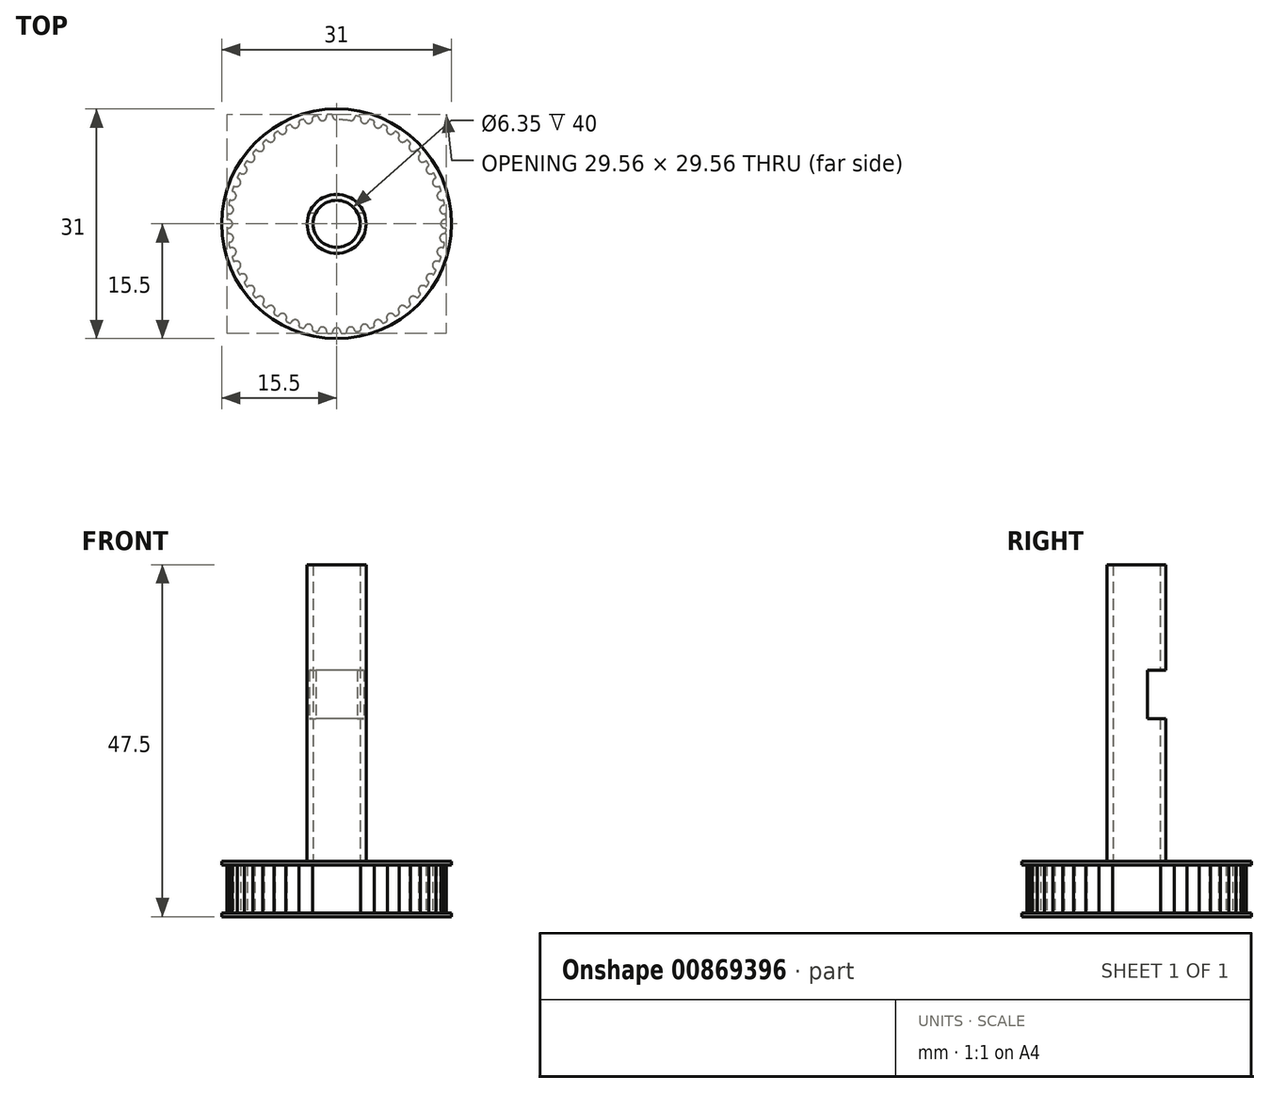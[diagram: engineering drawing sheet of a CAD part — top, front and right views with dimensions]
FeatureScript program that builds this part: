
annotation { "Feature Type Name" : "Feature", "Feature Type Description" : "" }
export const myFeature = defineFeature(function(context is Context, id is Id, definition is map)
    precondition{}
    {
        {
            var Q0;
            Q0=qCreatedBy(makeId("Top.planeOp"),FACE);
            var sketch = newSketch(context, id + "F0", { "sketchPlane" : qUnion([Q0])});
            skArc(sketch, "E0", {"start": v(-0.74, 14.78) * mm, "mid": v(-0.97, 14.77) * mm, "end": v(-1.2, 14.75) * mm});
            skCircle(sketch, "E1", {"center": v(0, 0) * mm, "radius": 14.05 * mm});
            skArc(sketch, "E2", {"start": v(-0.5, 14.37) * mm, "mid": v(-0.3, 14.14) * mm, "end": v(0, 14.05) * mm});
            skLineSegment(sketch, "E3", {"start": v(0, 0) * mm, "end": v(0.38, 14.04) * mm});
            skArc(sketch, "E4", {"start": v(-0.59, 14.65) * mm, "mid": v(-0.56, 14.5) * mm, "end": v(-0.5, 14.37) * mm});
            skArc(sketch, "E5", {"start": v(-0.59, 14.65) * mm, "mid": v(-0.64, 14.75) * mm, "end": v(-0.74, 14.78) * mm});
            skArc(sketch, "E6.MirrorCS", {"start": v(0.59, 14.65) * mm, "mid": v(0.64, 14.75) * mm, "end": v(0.74, 14.78) * mm});
            skArc(sketch, "E7.MirrorCS", {"start": v(0.59, 14.65) * mm, "mid": v(0.56, 14.5) * mm, "end": v(0.5, 14.37) * mm});
            skArc(sketch, "E8.MirrorCS", {"start": v(0.5, 14.37) * mm, "mid": v(0.3, 14.14) * mm, "end": v(0, 14.05) * mm});
            skArc(sketch, "E9.1.0", {"start": v(-2.5, 14.45) * mm, "mid": v(-2.56, 14.54) * mm, "end": v(-2.67, 14.56) * mm});
            skArc(sketch, "E9.1.1", {"start": v(-2.5, 14.45) * mm, "mid": v(-2.44, 14.31) * mm, "end": v(-2.37, 14.18) * mm});
            skArc(sketch, "E9.1.2", {"start": v(-2.37, 14.18) * mm, "mid": v(-2.14, 13.98) * mm, "end": v(-1.83, 13.93) * mm});
            skArc(sketch, "E9.1.3", {"start": v(-1.38, 14.31) * mm, "mid": v(-1.55, 14.05) * mm, "end": v(-1.83, 13.93) * mm});
            skArc(sketch, "E9.1.4", {"start": v(-1.33, 14.6) * mm, "mid": v(-1.34, 14.46) * mm, "end": v(-1.38, 14.31) * mm});
            skArc(sketch, "E9.1.5", {"start": v(-1.33, 14.6) * mm, "mid": v(-1.3, 14.7) * mm, "end": v(-1.2, 14.75) * mm});
            skArc(sketch, "E9.2.0", {"start": v(-4.36, 14) * mm, "mid": v(-4.44, 14.08) * mm, "end": v(-4.54, 14.09) * mm});
            skArc(sketch, "E9.2.1", {"start": v(-4.36, 14) * mm, "mid": v(-4.3, 13.87) * mm, "end": v(-4.2, 13.75) * mm});
            skArc(sketch, "E9.2.2", {"start": v(-4.2, 13.75) * mm, "mid": v(-3.95, 13.58) * mm, "end": v(-3.64, 13.57) * mm});
            skArc(sketch, "E9.2.3", {"start": v(-3.23, 14) * mm, "mid": v(-3.37, 13.73) * mm, "end": v(-3.64, 13.57) * mm});
            skArc(sketch, "E9.2.4", {"start": v(-3.23, 14.3) * mm, "mid": v(-3.22, 14.16) * mm, "end": v(-3.23, 14) * mm});
            skArc(sketch, "E9.2.5", {"start": v(-3.23, 14.3) * mm, "mid": v(-3.2, 14.41) * mm, "end": v(-3.1, 14.47) * mm});
            skArc(sketch, "E9.3.0", {"start": v(-6.15, 13.31) * mm, "mid": v(-6.24, 13.38) * mm, "end": v(-6.34, 13.37) * mm});
            skArc(sketch, "E9.3.1", {"start": v(-6.15, 13.31) * mm, "mid": v(-6.06, 13.2) * mm, "end": v(-5.96, 13.08) * mm});
            skArc(sketch, "E9.3.2", {"start": v(-5.96, 13.08) * mm, "mid": v(-5.68, 12.95) * mm, "end": v(-5.38, 12.98) * mm});
            skArc(sketch, "E9.3.3", {"start": v(-5.03, 13.47) * mm, "mid": v(-5.14, 13.17) * mm, "end": v(-5.38, 12.98) * mm});
            skArc(sketch, "E9.3.4", {"start": v(-5.06, 13.76) * mm, "mid": v(-5.04, 13.62) * mm, "end": v(-5.03, 13.47) * mm});
            skArc(sketch, "E9.3.5", {"start": v(-5.06, 13.76) * mm, "mid": v(-5.05, 13.87) * mm, "end": v(-4.97, 13.94) * mm});
            skArc(sketch, "E9.4.0", {"start": v(-7.83, 12.4) * mm, "mid": v(-7.93, 12.45) * mm, "end": v(-8.03, 12.43) * mm});
            skArc(sketch, "E9.4.1", {"start": v(-7.83, 12.4) * mm, "mid": v(-7.73, 12.29) * mm, "end": v(-7.62, 12.2) * mm});
            skArc(sketch, "E9.4.2", {"start": v(-7.62, 12.2) * mm, "mid": v(-7.33, 12.1) * mm, "end": v(-7.02, 12.17) * mm});
            skArc(sketch, "E9.4.3", {"start": v(-6.75, 12.7) * mm, "mid": v(-6.81, 12.4) * mm, "end": v(-7.02, 12.17) * mm});
            skArc(sketch, "E9.4.4", {"start": v(-6.82, 12.98) * mm, "mid": v(-6.77, 12.84) * mm, "end": v(-6.75, 12.7) * mm});
            skArc(sketch, "E9.4.5", {"start": v(-6.82, 12.98) * mm, "mid": v(-6.82, 13.1) * mm, "end": v(-6.75, 13.17) * mm});
            skArc(sketch, "E9.5.0", {"start": v(-9.39, 11.27) * mm, "mid": v(-9.49, 11.3) * mm, "end": v(-9.59, 11.27) * mm});
            skArc(sketch, "E9.5.1", {"start": v(-9.39, 11.27) * mm, "mid": v(-9.27, 11.17) * mm, "end": v(-9.15, 11.1) * mm});
            skArc(sketch, "E9.5.2", {"start": v(-9.15, 11.1) * mm, "mid": v(-8.84, 11.03) * mm, "end": v(-8.55, 11.15) * mm});
            skArc(sketch, "E9.5.3", {"start": v(-8.35, 11.7) * mm, "mid": v(-8.37, 11.4) * mm, "end": v(-8.55, 11.15) * mm});
            skArc(sketch, "E9.5.4", {"start": v(-8.45, 11.98) * mm, "mid": v(-8.4, 11.85) * mm, "end": v(-8.35, 11.7) * mm});
            skArc(sketch, "E9.5.5", {"start": v(-8.45, 11.98) * mm, "mid": v(-8.47, 12.09) * mm, "end": v(-8.4, 12.18) * mm});
            skArc(sketch, "E9.6.0", {"start": v(-10.78, 9.95) * mm, "mid": v(-10.88, 9.98) * mm, "end": v(-10.98, 9.93) * mm});
            skArc(sketch, "E9.6.1", {"start": v(-10.78, 9.95) * mm, "mid": v(-10.65, 9.87) * mm, "end": v(-10.52, 9.8) * mm});
            skArc(sketch, "E9.6.2", {"start": v(-10.52, 9.8) * mm, "mid": v(-10.2, 9.79) * mm, "end": v(-9.93, 9.93) * mm});
            skArc(sketch, "E9.6.3", {"start": v(-9.8, 10.52) * mm, "mid": v(-9.79, 10.2) * mm, "end": v(-9.93, 9.93) * mm});
            skArc(sketch, "E9.6.4", {"start": v(-9.95, 10.78) * mm, "mid": v(-9.87, 10.65) * mm, "end": v(-9.8, 10.52) * mm});
            skArc(sketch, "E9.6.5", {"start": v(-9.95, 10.78) * mm, "mid": v(-9.98, 10.88) * mm, "end": v(-9.93, 10.98) * mm});
            skArc(sketch, "E9.7.0", {"start": v(-11.98, 8.45) * mm, "mid": v(-12.09, 8.47) * mm, "end": v(-12.18, 8.4) * mm});
            skArc(sketch, "E9.7.1", {"start": v(-11.98, 8.45) * mm, "mid": v(-11.85, 8.4) * mm, "end": v(-11.7, 8.35) * mm});
            skArc(sketch, "E9.7.2", {"start": v(-11.7, 8.35) * mm, "mid": v(-11.4, 8.37) * mm, "end": v(-11.15, 8.55) * mm});
            skArc(sketch, "E9.7.3", {"start": v(-11.1, 9.15) * mm, "mid": v(-11.03, 8.84) * mm, "end": v(-11.15, 8.55) * mm});
            skArc(sketch, "E9.7.4", {"start": v(-11.27, 9.39) * mm, "mid": v(-11.17, 9.27) * mm, "end": v(-11.1, 9.15) * mm});
            skArc(sketch, "E9.7.5", {"start": v(-11.27, 9.39) * mm, "mid": v(-11.3, 9.49) * mm, "end": v(-11.27, 9.59) * mm});
            skArc(sketch, "E9.8.0", {"start": v(-12.98, 6.82) * mm, "mid": v(-13.1, 6.82) * mm, "end": v(-13.17, 6.75) * mm});
            skArc(sketch, "E9.8.1", {"start": v(-12.98, 6.82) * mm, "mid": v(-12.84, 6.77) * mm, "end": v(-12.7, 6.75) * mm});
            skArc(sketch, "E9.8.2", {"start": v(-12.7, 6.75) * mm, "mid": v(-12.4, 6.81) * mm, "end": v(-12.17, 7.03) * mm});
            skArc(sketch, "E9.8.3", {"start": v(-12.2, 7.62) * mm, "mid": v(-12.1, 7.33) * mm, "end": v(-12.17, 7.03) * mm});
            skArc(sketch, "E9.8.4", {"start": v(-12.4, 7.83) * mm, "mid": v(-12.29, 7.73) * mm, "end": v(-12.2, 7.62) * mm});
            skArc(sketch, "E9.8.5", {"start": v(-12.4, 7.83) * mm, "mid": v(-12.45, 7.93) * mm, "end": v(-12.43, 8.03) * mm});
            skArc(sketch, "E9.9.0", {"start": v(-13.76, 5.06) * mm, "mid": v(-13.87, 5.05) * mm, "end": v(-13.94, 4.97) * mm});
            skArc(sketch, "E9.9.1", {"start": v(-13.76, 5.06) * mm, "mid": v(-13.62, 5.04) * mm, "end": v(-13.47, 5.03) * mm});
            skArc(sketch, "E9.9.2", {"start": v(-13.47, 5.03) * mm, "mid": v(-13.17, 5.14) * mm, "end": v(-12.98, 5.38) * mm});
            skArc(sketch, "E9.9.3", {"start": v(-13.08, 5.96) * mm, "mid": v(-12.95, 5.68) * mm, "end": v(-12.98, 5.38) * mm});
            skArc(sketch, "E9.9.4", {"start": v(-13.31, 6.15) * mm, "mid": v(-13.2, 6.06) * mm, "end": v(-13.08, 5.96) * mm});
            skArc(sketch, "E9.9.5", {"start": v(-13.31, 6.15) * mm, "mid": v(-13.38, 6.24) * mm, "end": v(-13.37, 6.34) * mm});
            skArc(sketch, "E9.10.0", {"start": v(-14.3, 3.23) * mm, "mid": v(-14.41, 3.2) * mm, "end": v(-14.47, 3.1) * mm});
            skArc(sketch, "E9.10.1", {"start": v(-14.3, 3.23) * mm, "mid": v(-14.16, 3.22) * mm, "end": v(-14, 3.23) * mm});
            skArc(sketch, "E9.10.2", {"start": v(-14, 3.23) * mm, "mid": v(-13.73, 3.37) * mm, "end": v(-13.57, 3.64) * mm});
            skArc(sketch, "E9.10.3", {"start": v(-13.75, 4.2) * mm, "mid": v(-13.58, 3.95) * mm, "end": v(-13.57, 3.64) * mm});
            skArc(sketch, "E9.10.4", {"start": v(-14, 4.36) * mm, "mid": v(-13.87, 4.3) * mm, "end": v(-13.75, 4.2) * mm});
            skArc(sketch, "E9.10.5", {"start": v(-14, 4.36) * mm, "mid": v(-14.08, 4.44) * mm, "end": v(-14.09, 4.54) * mm});
            skArc(sketch, "E9.11.0", {"start": v(-14.6, 1.33) * mm, "mid": v(-14.7, 1.3) * mm, "end": v(-14.75, 1.2) * mm});
            skArc(sketch, "E9.11.1", {"start": v(-14.6, 1.33) * mm, "mid": v(-14.46, 1.34) * mm, "end": v(-14.31, 1.38) * mm});
            skArc(sketch, "E9.11.2", {"start": v(-14.31, 1.38) * mm, "mid": v(-14.05, 1.55) * mm, "end": v(-13.93, 1.83) * mm});
            skArc(sketch, "E9.11.3", {"start": v(-14.18, 2.37) * mm, "mid": v(-13.98, 2.14) * mm, "end": v(-13.93, 1.83) * mm});
            skArc(sketch, "E9.11.4", {"start": v(-14.45, 2.5) * mm, "mid": v(-14.31, 2.44) * mm, "end": v(-14.18, 2.37) * mm});
            skArc(sketch, "E9.11.5", {"start": v(-14.45, 2.5) * mm, "mid": v(-14.54, 2.56) * mm, "end": v(-14.56, 2.67) * mm});
            skArc(sketch, "E9.12.0", {"start": v(-14.65, -0.59) * mm, "mid": v(-14.75, -0.64) * mm, "end": v(-14.78, -0.74) * mm});
            skArc(sketch, "E9.12.1", {"start": v(-14.65, -0.59) * mm, "mid": v(-14.5, -0.56) * mm, "end": v(-14.37, -0.5) * mm});
            skArc(sketch, "E9.12.2", {"start": v(-14.37, -0.5) * mm, "mid": v(-14.14, -0.3) * mm, "end": v(-14.05, 0) * mm});
            skArc(sketch, "E9.12.3", {"start": v(-14.37, 0.5) * mm, "mid": v(-14.14, 0.3) * mm, "end": v(-14.05, 0) * mm});
            skArc(sketch, "E9.12.4", {"start": v(-14.65, 0.59) * mm, "mid": v(-14.5, 0.56) * mm, "end": v(-14.37, 0.5) * mm});
            skArc(sketch, "E9.12.5", {"start": v(-14.65, 0.59) * mm, "mid": v(-14.75, 0.64) * mm, "end": v(-14.78, 0.74) * mm});
            skArc(sketch, "E9.13.0", {"start": v(-14.45, -2.5) * mm, "mid": v(-14.54, -2.56) * mm, "end": v(-14.56, -2.67) * mm});
            skArc(sketch, "E9.13.1", {"start": v(-14.45, -2.5) * mm, "mid": v(-14.31, -2.44) * mm, "end": v(-14.18, -2.37) * mm});
            skArc(sketch, "E9.13.2", {"start": v(-14.18, -2.37) * mm, "mid": v(-13.98, -2.14) * mm, "end": v(-13.93, -1.83) * mm});
            skArc(sketch, "E9.13.3", {"start": v(-14.31, -1.38) * mm, "mid": v(-14.05, -1.55) * mm, "end": v(-13.93, -1.83) * mm});
            skArc(sketch, "E9.13.4", {"start": v(-14.6, -1.33) * mm, "mid": v(-14.46, -1.34) * mm, "end": v(-14.31, -1.38) * mm});
            skArc(sketch, "E9.13.5", {"start": v(-14.6, -1.33) * mm, "mid": v(-14.7, -1.3) * mm, "end": v(-14.75, -1.2) * mm});
            skArc(sketch, "E9.14.0", {"start": v(-14, -4.36) * mm, "mid": v(-14.08, -4.44) * mm, "end": v(-14.09, -4.54) * mm});
            skArc(sketch, "E9.14.1", {"start": v(-14, -4.36) * mm, "mid": v(-13.87, -4.3) * mm, "end": v(-13.75, -4.2) * mm});
            skArc(sketch, "E9.14.2", {"start": v(-13.75, -4.2) * mm, "mid": v(-13.58, -3.95) * mm, "end": v(-13.57, -3.64) * mm});
            skArc(sketch, "E9.14.3", {"start": v(-14, -3.23) * mm, "mid": v(-13.73, -3.37) * mm, "end": v(-13.57, -3.64) * mm});
            skArc(sketch, "E9.14.4", {"start": v(-14.3, -3.23) * mm, "mid": v(-14.16, -3.22) * mm, "end": v(-14, -3.23) * mm});
            skArc(sketch, "E9.14.5", {"start": v(-14.3, -3.23) * mm, "mid": v(-14.41, -3.2) * mm, "end": v(-14.47, -3.1) * mm});
            skArc(sketch, "E9.15.0", {"start": v(-13.31, -6.15) * mm, "mid": v(-13.38, -6.24) * mm, "end": v(-13.37, -6.34) * mm});
            skArc(sketch, "E9.15.1", {"start": v(-13.31, -6.15) * mm, "mid": v(-13.2, -6.06) * mm, "end": v(-13.08, -5.96) * mm});
            skArc(sketch, "E9.15.2", {"start": v(-13.08, -5.96) * mm, "mid": v(-12.95, -5.68) * mm, "end": v(-12.98, -5.38) * mm});
            skArc(sketch, "E9.15.3", {"start": v(-13.47, -5.03) * mm, "mid": v(-13.17, -5.14) * mm, "end": v(-12.98, -5.38) * mm});
            skArc(sketch, "E9.15.4", {"start": v(-13.76, -5.06) * mm, "mid": v(-13.62, -5.04) * mm, "end": v(-13.47, -5.03) * mm});
            skArc(sketch, "E9.15.5", {"start": v(-13.76, -5.06) * mm, "mid": v(-13.87, -5.05) * mm, "end": v(-13.94, -4.97) * mm});
            skArc(sketch, "E9.16.0", {"start": v(-12.4, -7.83) * mm, "mid": v(-12.45, -7.93) * mm, "end": v(-12.43, -8.03) * mm});
            skArc(sketch, "E9.16.1", {"start": v(-12.4, -7.83) * mm, "mid": v(-12.29, -7.73) * mm, "end": v(-12.2, -7.62) * mm});
            skArc(sketch, "E9.16.2", {"start": v(-12.2, -7.62) * mm, "mid": v(-12.1, -7.33) * mm, "end": v(-12.17, -7.02) * mm});
            skArc(sketch, "E9.16.3", {"start": v(-12.7, -6.75) * mm, "mid": v(-12.4, -6.81) * mm, "end": v(-12.17, -7.02) * mm});
            skArc(sketch, "E9.16.4", {"start": v(-12.98, -6.82) * mm, "mid": v(-12.84, -6.77) * mm, "end": v(-12.7, -6.75) * mm});
            skArc(sketch, "E9.16.5", {"start": v(-12.98, -6.82) * mm, "mid": v(-13.1, -6.82) * mm, "end": v(-13.17, -6.75) * mm});
            skArc(sketch, "E9.17.0", {"start": v(-11.27, -9.39) * mm, "mid": v(-11.3, -9.49) * mm, "end": v(-11.27, -9.59) * mm});
            skArc(sketch, "E9.17.1", {"start": v(-11.27, -9.39) * mm, "mid": v(-11.17, -9.27) * mm, "end": v(-11.1, -9.15) * mm});
            skArc(sketch, "E9.17.2", {"start": v(-11.1, -9.15) * mm, "mid": v(-11.03, -8.84) * mm, "end": v(-11.15, -8.55) * mm});
            skArc(sketch, "E9.17.3", {"start": v(-11.7, -8.35) * mm, "mid": v(-11.4, -8.37) * mm, "end": v(-11.15, -8.55) * mm});
            skArc(sketch, "E9.17.4", {"start": v(-11.98, -8.45) * mm, "mid": v(-11.85, -8.4) * mm, "end": v(-11.7, -8.35) * mm});
            skArc(sketch, "E9.17.5", {"start": v(-11.98, -8.45) * mm, "mid": v(-12.09, -8.47) * mm, "end": v(-12.18, -8.4) * mm});
            skArc(sketch, "E9.18.0", {"start": v(-9.95, -10.78) * mm, "mid": v(-9.98, -10.88) * mm, "end": v(-9.93, -10.98) * mm});
            skArc(sketch, "E9.18.1", {"start": v(-9.95, -10.78) * mm, "mid": v(-9.87, -10.65) * mm, "end": v(-9.8, -10.52) * mm});
            skArc(sketch, "E9.18.2", {"start": v(-9.8, -10.52) * mm, "mid": v(-9.79, -10.2) * mm, "end": v(-9.93, -9.93) * mm});
            skArc(sketch, "E9.18.3", {"start": v(-10.52, -9.8) * mm, "mid": v(-10.2, -9.79) * mm, "end": v(-9.93, -9.93) * mm});
            skArc(sketch, "E9.18.4", {"start": v(-10.78, -9.95) * mm, "mid": v(-10.65, -9.87) * mm, "end": v(-10.52, -9.8) * mm});
            skArc(sketch, "E9.18.5", {"start": v(-10.78, -9.95) * mm, "mid": v(-10.88, -9.98) * mm, "end": v(-10.98, -9.93) * mm});
            skArc(sketch, "E9.19.0", {"start": v(-8.45, -11.98) * mm, "mid": v(-8.47, -12.09) * mm, "end": v(-8.4, -12.18) * mm});
            skArc(sketch, "E9.19.1", {"start": v(-8.45, -11.98) * mm, "mid": v(-8.4, -11.85) * mm, "end": v(-8.35, -11.7) * mm});
            skArc(sketch, "E9.19.2", {"start": v(-8.35, -11.7) * mm, "mid": v(-8.37, -11.4) * mm, "end": v(-8.55, -11.15) * mm});
            skArc(sketch, "E9.19.3", {"start": v(-9.15, -11.1) * mm, "mid": v(-8.84, -11.03) * mm, "end": v(-8.55, -11.15) * mm});
            skArc(sketch, "E9.19.4", {"start": v(-9.39, -11.27) * mm, "mid": v(-9.27, -11.17) * mm, "end": v(-9.15, -11.1) * mm});
            skArc(sketch, "E9.19.5", {"start": v(-9.39, -11.27) * mm, "mid": v(-9.49, -11.3) * mm, "end": v(-9.59, -11.27) * mm});
            skArc(sketch, "E9.20.0", {"start": v(-6.82, -12.98) * mm, "mid": v(-6.82, -13.1) * mm, "end": v(-6.75, -13.17) * mm});
            skArc(sketch, "E9.20.1", {"start": v(-6.82, -12.98) * mm, "mid": v(-6.77, -12.84) * mm, "end": v(-6.75, -12.7) * mm});
            skArc(sketch, "E9.20.2", {"start": v(-6.75, -12.7) * mm, "mid": v(-6.81, -12.4) * mm, "end": v(-7.02, -12.17) * mm});
            skArc(sketch, "E9.20.3", {"start": v(-7.62, -12.2) * mm, "mid": v(-7.33, -12.1) * mm, "end": v(-7.02, -12.17) * mm});
            skArc(sketch, "E9.20.4", {"start": v(-7.83, -12.4) * mm, "mid": v(-7.73, -12.29) * mm, "end": v(-7.62, -12.2) * mm});
            skArc(sketch, "E9.20.5", {"start": v(-7.83, -12.4) * mm, "mid": v(-7.93, -12.45) * mm, "end": v(-8.03, -12.43) * mm});
            skArc(sketch, "E9.21.0", {"start": v(-5.06, -13.76) * mm, "mid": v(-5.05, -13.87) * mm, "end": v(-4.97, -13.94) * mm});
            skArc(sketch, "E9.21.1", {"start": v(-5.06, -13.76) * mm, "mid": v(-5.04, -13.62) * mm, "end": v(-5.03, -13.47) * mm});
            skArc(sketch, "E9.21.2", {"start": v(-5.03, -13.47) * mm, "mid": v(-5.14, -13.17) * mm, "end": v(-5.38, -12.98) * mm});
            skArc(sketch, "E9.21.3", {"start": v(-5.96, -13.08) * mm, "mid": v(-5.68, -12.95) * mm, "end": v(-5.38, -12.98) * mm});
            skArc(sketch, "E9.21.4", {"start": v(-6.15, -13.31) * mm, "mid": v(-6.06, -13.2) * mm, "end": v(-5.96, -13.08) * mm});
            skArc(sketch, "E9.21.5", {"start": v(-6.15, -13.31) * mm, "mid": v(-6.24, -13.38) * mm, "end": v(-6.34, -13.37) * mm});
            skArc(sketch, "E9.22.0", {"start": v(-3.23, -14.3) * mm, "mid": v(-3.2, -14.41) * mm, "end": v(-3.1, -14.47) * mm});
            skArc(sketch, "E9.22.1", {"start": v(-3.23, -14.3) * mm, "mid": v(-3.22, -14.16) * mm, "end": v(-3.23, -14) * mm});
            skArc(sketch, "E9.22.2", {"start": v(-3.23, -14) * mm, "mid": v(-3.37, -13.73) * mm, "end": v(-3.64, -13.57) * mm});
            skArc(sketch, "E9.22.3", {"start": v(-4.2, -13.75) * mm, "mid": v(-3.95, -13.58) * mm, "end": v(-3.64, -13.57) * mm});
            skArc(sketch, "E9.22.4", {"start": v(-4.36, -14) * mm, "mid": v(-4.3, -13.87) * mm, "end": v(-4.2, -13.75) * mm});
            skArc(sketch, "E9.22.5", {"start": v(-4.36, -14) * mm, "mid": v(-4.44, -14.08) * mm, "end": v(-4.54, -14.09) * mm});
            skArc(sketch, "E9.23.0", {"start": v(-1.33, -14.6) * mm, "mid": v(-1.3, -14.7) * mm, "end": v(-1.2, -14.75) * mm});
            skArc(sketch, "E9.23.1", {"start": v(-1.33, -14.6) * mm, "mid": v(-1.34, -14.46) * mm, "end": v(-1.38, -14.31) * mm});
            skArc(sketch, "E9.23.2", {"start": v(-1.38, -14.31) * mm, "mid": v(-1.55, -14.05) * mm, "end": v(-1.83, -13.93) * mm});
            skArc(sketch, "E9.23.3", {"start": v(-2.37, -14.18) * mm, "mid": v(-2.14, -13.98) * mm, "end": v(-1.83, -13.93) * mm});
            skArc(sketch, "E9.23.4", {"start": v(-2.5, -14.45) * mm, "mid": v(-2.44, -14.31) * mm, "end": v(-2.37, -14.18) * mm});
            skArc(sketch, "E9.23.5", {"start": v(-2.5, -14.45) * mm, "mid": v(-2.56, -14.54) * mm, "end": v(-2.67, -14.56) * mm});
            skArc(sketch, "E9.24.0", {"start": v(0.59, -14.65) * mm, "mid": v(0.64, -14.75) * mm, "end": v(0.74, -14.78) * mm});
            skArc(sketch, "E9.24.1", {"start": v(0.59, -14.65) * mm, "mid": v(0.56, -14.5) * mm, "end": v(0.5, -14.37) * mm});
            skArc(sketch, "E9.24.2", {"start": v(0.5, -14.37) * mm, "mid": v(0.3, -14.14) * mm, "end": v(0, -14.05) * mm});
            skArc(sketch, "E9.24.3", {"start": v(-0.5, -14.37) * mm, "mid": v(-0.3, -14.14) * mm, "end": v(0, -14.05) * mm});
            skArc(sketch, "E9.24.4", {"start": v(-0.59, -14.65) * mm, "mid": v(-0.56, -14.5) * mm, "end": v(-0.5, -14.37) * mm});
            skArc(sketch, "E9.24.5", {"start": v(-0.59, -14.65) * mm, "mid": v(-0.64, -14.75) * mm, "end": v(-0.74, -14.78) * mm});
            skArc(sketch, "E9.25.0", {"start": v(2.5, -14.45) * mm, "mid": v(2.56, -14.54) * mm, "end": v(2.67, -14.56) * mm});
            skArc(sketch, "E9.25.1", {"start": v(2.5, -14.45) * mm, "mid": v(2.44, -14.31) * mm, "end": v(2.37, -14.18) * mm});
            skArc(sketch, "E9.25.2", {"start": v(2.37, -14.18) * mm, "mid": v(2.14, -13.98) * mm, "end": v(1.83, -13.93) * mm});
            skArc(sketch, "E9.25.3", {"start": v(1.38, -14.31) * mm, "mid": v(1.55, -14.05) * mm, "end": v(1.83, -13.93) * mm});
            skArc(sketch, "E9.25.4", {"start": v(1.33, -14.6) * mm, "mid": v(1.34, -14.46) * mm, "end": v(1.38, -14.31) * mm});
            skArc(sketch, "E9.25.5", {"start": v(1.33, -14.6) * mm, "mid": v(1.3, -14.7) * mm, "end": v(1.2, -14.75) * mm});
            skArc(sketch, "E9.26.0", {"start": v(4.36, -14) * mm, "mid": v(4.44, -14.08) * mm, "end": v(4.54, -14.09) * mm});
            skArc(sketch, "E9.26.1", {"start": v(4.36, -14) * mm, "mid": v(4.3, -13.87) * mm, "end": v(4.2, -13.75) * mm});
            skArc(sketch, "E9.26.2", {"start": v(4.2, -13.75) * mm, "mid": v(3.95, -13.58) * mm, "end": v(3.64, -13.57) * mm});
            skArc(sketch, "E9.26.3", {"start": v(3.23, -14) * mm, "mid": v(3.37, -13.73) * mm, "end": v(3.64, -13.57) * mm});
            skArc(sketch, "E9.26.4", {"start": v(3.23, -14.3) * mm, "mid": v(3.22, -14.16) * mm, "end": v(3.23, -14) * mm});
            skArc(sketch, "E9.26.5", {"start": v(3.23, -14.3) * mm, "mid": v(3.2, -14.41) * mm, "end": v(3.1, -14.47) * mm});
            skArc(sketch, "E9.27.0", {"start": v(6.15, -13.31) * mm, "mid": v(6.24, -13.38) * mm, "end": v(6.34, -13.37) * mm});
            skArc(sketch, "E9.27.1", {"start": v(6.15, -13.31) * mm, "mid": v(6.06, -13.2) * mm, "end": v(5.96, -13.08) * mm});
            skArc(sketch, "E9.27.2", {"start": v(5.96, -13.08) * mm, "mid": v(5.68, -12.95) * mm, "end": v(5.38, -12.98) * mm});
            skArc(sketch, "E9.27.3", {"start": v(5.03, -13.47) * mm, "mid": v(5.14, -13.17) * mm, "end": v(5.38, -12.98) * mm});
            skArc(sketch, "E9.27.4", {"start": v(5.06, -13.76) * mm, "mid": v(5.04, -13.62) * mm, "end": v(5.03, -13.47) * mm});
            skArc(sketch, "E9.27.5", {"start": v(5.06, -13.76) * mm, "mid": v(5.05, -13.87) * mm, "end": v(4.97, -13.94) * mm});
            skArc(sketch, "E9.28.0", {"start": v(7.83, -12.4) * mm, "mid": v(7.93, -12.45) * mm, "end": v(8.03, -12.43) * mm});
            skArc(sketch, "E9.28.1", {"start": v(7.83, -12.4) * mm, "mid": v(7.73, -12.29) * mm, "end": v(7.62, -12.2) * mm});
            skArc(sketch, "E9.28.2", {"start": v(7.62, -12.2) * mm, "mid": v(7.33, -12.1) * mm, "end": v(7.02, -12.17) * mm});
            skArc(sketch, "E9.28.3", {"start": v(6.75, -12.7) * mm, "mid": v(6.81, -12.4) * mm, "end": v(7.02, -12.17) * mm});
            skArc(sketch, "E9.28.4", {"start": v(6.82, -12.98) * mm, "mid": v(6.77, -12.84) * mm, "end": v(6.75, -12.7) * mm});
            skArc(sketch, "E9.28.5", {"start": v(6.82, -12.98) * mm, "mid": v(6.82, -13.1) * mm, "end": v(6.75, -13.17) * mm});
            skArc(sketch, "E9.29.0", {"start": v(9.39, -11.27) * mm, "mid": v(9.49, -11.3) * mm, "end": v(9.59, -11.27) * mm});
            skArc(sketch, "E9.29.1", {"start": v(9.39, -11.27) * mm, "mid": v(9.27, -11.17) * mm, "end": v(9.15, -11.1) * mm});
            skArc(sketch, "E9.29.2", {"start": v(9.15, -11.1) * mm, "mid": v(8.84, -11.03) * mm, "end": v(8.55, -11.15) * mm});
            skArc(sketch, "E9.29.3", {"start": v(8.35, -11.7) * mm, "mid": v(8.37, -11.4) * mm, "end": v(8.55, -11.15) * mm});
            skArc(sketch, "E9.29.4", {"start": v(8.45, -11.98) * mm, "mid": v(8.4, -11.85) * mm, "end": v(8.35, -11.7) * mm});
            skArc(sketch, "E9.29.5", {"start": v(8.45, -11.98) * mm, "mid": v(8.47, -12.09) * mm, "end": v(8.4, -12.18) * mm});
            skArc(sketch, "E9.30.0", {"start": v(10.78, -9.95) * mm, "mid": v(10.88, -9.98) * mm, "end": v(10.98, -9.93) * mm});
            skArc(sketch, "E9.30.1", {"start": v(10.78, -9.95) * mm, "mid": v(10.65, -9.87) * mm, "end": v(10.52, -9.8) * mm});
            skArc(sketch, "E9.30.2", {"start": v(10.52, -9.8) * mm, "mid": v(10.2, -9.79) * mm, "end": v(9.93, -9.93) * mm});
            skArc(sketch, "E9.30.3", {"start": v(9.8, -10.52) * mm, "mid": v(9.79, -10.2) * mm, "end": v(9.93, -9.93) * mm});
            skArc(sketch, "E9.30.4", {"start": v(9.95, -10.78) * mm, "mid": v(9.87, -10.65) * mm, "end": v(9.8, -10.52) * mm});
            skArc(sketch, "E9.30.5", {"start": v(9.95, -10.78) * mm, "mid": v(9.98, -10.88) * mm, "end": v(9.93, -10.98) * mm});
            skArc(sketch, "E9.31.0", {"start": v(11.98, -8.45) * mm, "mid": v(12.09, -8.47) * mm, "end": v(12.18, -8.4) * mm});
            skArc(sketch, "E9.31.1", {"start": v(11.98, -8.45) * mm, "mid": v(11.85, -8.4) * mm, "end": v(11.7, -8.35) * mm});
            skArc(sketch, "E9.31.2", {"start": v(11.7, -8.35) * mm, "mid": v(11.4, -8.37) * mm, "end": v(11.15, -8.55) * mm});
            skArc(sketch, "E9.31.3", {"start": v(11.1, -9.15) * mm, "mid": v(11.03, -8.84) * mm, "end": v(11.15, -8.55) * mm});
            skArc(sketch, "E9.31.4", {"start": v(11.27, -9.39) * mm, "mid": v(11.17, -9.27) * mm, "end": v(11.1, -9.15) * mm});
            skArc(sketch, "E9.31.5", {"start": v(11.27, -9.39) * mm, "mid": v(11.3, -9.49) * mm, "end": v(11.27, -9.59) * mm});
            skArc(sketch, "E9.32.0", {"start": v(12.98, -6.82) * mm, "mid": v(13.1, -6.82) * mm, "end": v(13.17, -6.75) * mm});
            skArc(sketch, "E9.32.1", {"start": v(12.98, -6.82) * mm, "mid": v(12.84, -6.77) * mm, "end": v(12.7, -6.75) * mm});
            skArc(sketch, "E9.32.2", {"start": v(12.7, -6.75) * mm, "mid": v(12.4, -6.81) * mm, "end": v(12.17, -7.03) * mm});
            skArc(sketch, "E9.32.3", {"start": v(12.2, -7.62) * mm, "mid": v(12.1, -7.33) * mm, "end": v(12.17, -7.03) * mm});
            skArc(sketch, "E9.32.4", {"start": v(12.4, -7.83) * mm, "mid": v(12.29, -7.73) * mm, "end": v(12.2, -7.62) * mm});
            skArc(sketch, "E9.32.5", {"start": v(12.4, -7.83) * mm, "mid": v(12.45, -7.93) * mm, "end": v(12.43, -8.03) * mm});
            skArc(sketch, "E9.33.0", {"start": v(13.76, -5.06) * mm, "mid": v(13.87, -5.05) * mm, "end": v(13.94, -4.97) * mm});
            skArc(sketch, "E9.33.1", {"start": v(13.76, -5.06) * mm, "mid": v(13.62, -5.04) * mm, "end": v(13.47, -5.03) * mm});
            skArc(sketch, "E9.33.2", {"start": v(13.47, -5.03) * mm, "mid": v(13.17, -5.14) * mm, "end": v(12.98, -5.38) * mm});
            skArc(sketch, "E9.33.3", {"start": v(13.08, -5.96) * mm, "mid": v(12.95, -5.68) * mm, "end": v(12.98, -5.38) * mm});
            skArc(sketch, "E9.33.4", {"start": v(13.31, -6.15) * mm, "mid": v(13.2, -6.06) * mm, "end": v(13.08, -5.96) * mm});
            skArc(sketch, "E9.33.5", {"start": v(13.31, -6.15) * mm, "mid": v(13.38, -6.24) * mm, "end": v(13.37, -6.34) * mm});
            skArc(sketch, "E9.34.0", {"start": v(14.3, -3.23) * mm, "mid": v(14.41, -3.2) * mm, "end": v(14.47, -3.1) * mm});
            skArc(sketch, "E9.34.1", {"start": v(14.3, -3.23) * mm, "mid": v(14.16, -3.22) * mm, "end": v(14, -3.23) * mm});
            skArc(sketch, "E9.34.2", {"start": v(14, -3.23) * mm, "mid": v(13.73, -3.37) * mm, "end": v(13.57, -3.64) * mm});
            skArc(sketch, "E9.34.3", {"start": v(13.75, -4.2) * mm, "mid": v(13.58, -3.95) * mm, "end": v(13.57, -3.64) * mm});
            skArc(sketch, "E9.34.4", {"start": v(14, -4.36) * mm, "mid": v(13.87, -4.3) * mm, "end": v(13.75, -4.2) * mm});
            skArc(sketch, "E9.34.5", {"start": v(14, -4.36) * mm, "mid": v(14.08, -4.44) * mm, "end": v(14.09, -4.54) * mm});
            skArc(sketch, "E9.35.0", {"start": v(14.6, -1.33) * mm, "mid": v(14.7, -1.3) * mm, "end": v(14.75, -1.2) * mm});
            skArc(sketch, "E9.35.1", {"start": v(14.6, -1.33) * mm, "mid": v(14.46, -1.34) * mm, "end": v(14.31, -1.38) * mm});
            skArc(sketch, "E9.35.2", {"start": v(14.31, -1.38) * mm, "mid": v(14.05, -1.55) * mm, "end": v(13.93, -1.83) * mm});
            skArc(sketch, "E9.35.3", {"start": v(14.18, -2.37) * mm, "mid": v(13.98, -2.14) * mm, "end": v(13.93, -1.83) * mm});
            skArc(sketch, "E9.35.4", {"start": v(14.45, -2.5) * mm, "mid": v(14.31, -2.44) * mm, "end": v(14.18, -2.37) * mm});
            skArc(sketch, "E9.35.5", {"start": v(14.45, -2.5) * mm, "mid": v(14.54, -2.56) * mm, "end": v(14.56, -2.67) * mm});
            skArc(sketch, "E9.36.0", {"start": v(14.65, 0.59) * mm, "mid": v(14.75, 0.64) * mm, "end": v(14.78, 0.74) * mm});
            skArc(sketch, "E9.36.1", {"start": v(14.65, 0.59) * mm, "mid": v(14.5, 0.56) * mm, "end": v(14.37, 0.5) * mm});
            skArc(sketch, "E9.36.2", {"start": v(14.37, 0.5) * mm, "mid": v(14.14, 0.3) * mm, "end": v(14.05, 0) * mm});
            skArc(sketch, "E9.36.3", {"start": v(14.37, -0.5) * mm, "mid": v(14.14, -0.3) * mm, "end": v(14.05, 0) * mm});
            skArc(sketch, "E9.36.4", {"start": v(14.65, -0.59) * mm, "mid": v(14.5, -0.56) * mm, "end": v(14.37, -0.5) * mm});
            skArc(sketch, "E9.36.5", {"start": v(14.65, -0.59) * mm, "mid": v(14.75, -0.64) * mm, "end": v(14.78, -0.74) * mm});
            skArc(sketch, "E9.37.0", {"start": v(14.45, 2.5) * mm, "mid": v(14.54, 2.56) * mm, "end": v(14.56, 2.67) * mm});
            skArc(sketch, "E9.37.1", {"start": v(14.45, 2.5) * mm, "mid": v(14.31, 2.44) * mm, "end": v(14.18, 2.37) * mm});
            skArc(sketch, "E9.37.2", {"start": v(14.18, 2.37) * mm, "mid": v(13.98, 2.14) * mm, "end": v(13.93, 1.83) * mm});
            skArc(sketch, "E9.37.3", {"start": v(14.31, 1.38) * mm, "mid": v(14.05, 1.55) * mm, "end": v(13.93, 1.83) * mm});
            skArc(sketch, "E9.37.4", {"start": v(14.6, 1.33) * mm, "mid": v(14.46, 1.34) * mm, "end": v(14.31, 1.38) * mm});
            skArc(sketch, "E9.37.5", {"start": v(14.6, 1.33) * mm, "mid": v(14.7, 1.3) * mm, "end": v(14.75, 1.2) * mm});
            skArc(sketch, "E9.38.0", {"start": v(14, 4.36) * mm, "mid": v(14.08, 4.44) * mm, "end": v(14.09, 4.54) * mm});
            skArc(sketch, "E9.38.1", {"start": v(14, 4.36) * mm, "mid": v(13.87, 4.3) * mm, "end": v(13.75, 4.2) * mm});
            skArc(sketch, "E9.38.2", {"start": v(13.75, 4.2) * mm, "mid": v(13.58, 3.95) * mm, "end": v(13.57, 3.64) * mm});
            skArc(sketch, "E9.38.3", {"start": v(14, 3.23) * mm, "mid": v(13.73, 3.37) * mm, "end": v(13.57, 3.64) * mm});
            skArc(sketch, "E9.38.4", {"start": v(14.3, 3.23) * mm, "mid": v(14.16, 3.22) * mm, "end": v(14, 3.23) * mm});
            skArc(sketch, "E9.38.5", {"start": v(14.3, 3.23) * mm, "mid": v(14.41, 3.2) * mm, "end": v(14.47, 3.1) * mm});
            skArc(sketch, "E9.39.0", {"start": v(13.31, 6.15) * mm, "mid": v(13.38, 6.24) * mm, "end": v(13.37, 6.34) * mm});
            skArc(sketch, "E9.39.1", {"start": v(13.31, 6.15) * mm, "mid": v(13.2, 6.06) * mm, "end": v(13.08, 5.96) * mm});
            skArc(sketch, "E9.39.2", {"start": v(13.08, 5.96) * mm, "mid": v(12.95, 5.68) * mm, "end": v(12.98, 5.38) * mm});
            skArc(sketch, "E9.39.3", {"start": v(13.47, 5.03) * mm, "mid": v(13.17, 5.14) * mm, "end": v(12.98, 5.38) * mm});
            skArc(sketch, "E9.39.4", {"start": v(13.76, 5.06) * mm, "mid": v(13.62, 5.04) * mm, "end": v(13.47, 5.03) * mm});
            skArc(sketch, "E9.39.5", {"start": v(13.76, 5.06) * mm, "mid": v(13.87, 5.05) * mm, "end": v(13.94, 4.97) * mm});
            skArc(sketch, "E9.40.0", {"start": v(12.4, 7.83) * mm, "mid": v(12.45, 7.93) * mm, "end": v(12.43, 8.03) * mm});
            skArc(sketch, "E9.40.1", {"start": v(12.4, 7.83) * mm, "mid": v(12.29, 7.73) * mm, "end": v(12.2, 7.62) * mm});
            skArc(sketch, "E9.40.2", {"start": v(12.2, 7.62) * mm, "mid": v(12.1, 7.33) * mm, "end": v(12.17, 7.03) * mm});
            skArc(sketch, "E9.40.3", {"start": v(12.7, 6.75) * mm, "mid": v(12.4, 6.81) * mm, "end": v(12.17, 7.03) * mm});
            skArc(sketch, "E9.40.4", {"start": v(12.98, 6.82) * mm, "mid": v(12.84, 6.77) * mm, "end": v(12.7, 6.75) * mm});
            skArc(sketch, "E9.40.5", {"start": v(12.98, 6.82) * mm, "mid": v(13.1, 6.82) * mm, "end": v(13.17, 6.75) * mm});
            skArc(sketch, "E9.41.0", {"start": v(11.27, 9.39) * mm, "mid": v(11.3, 9.49) * mm, "end": v(11.27, 9.59) * mm});
            skArc(sketch, "E9.41.1", {"start": v(11.27, 9.39) * mm, "mid": v(11.17, 9.27) * mm, "end": v(11.1, 9.15) * mm});
            skArc(sketch, "E9.41.2", {"start": v(11.1, 9.15) * mm, "mid": v(11.03, 8.84) * mm, "end": v(11.15, 8.55) * mm});
            skArc(sketch, "E9.41.3", {"start": v(11.7, 8.35) * mm, "mid": v(11.4, 8.37) * mm, "end": v(11.15, 8.55) * mm});
            skArc(sketch, "E9.41.4", {"start": v(11.98, 8.45) * mm, "mid": v(11.85, 8.4) * mm, "end": v(11.7, 8.35) * mm});
            skArc(sketch, "E9.41.5", {"start": v(11.98, 8.45) * mm, "mid": v(12.09, 8.47) * mm, "end": v(12.18, 8.4) * mm});
            skArc(sketch, "E9.42.0", {"start": v(9.95, 10.78) * mm, "mid": v(9.98, 10.88) * mm, "end": v(9.93, 10.98) * mm});
            skArc(sketch, "E9.42.1", {"start": v(9.95, 10.78) * mm, "mid": v(9.87, 10.65) * mm, "end": v(9.8, 10.52) * mm});
            skArc(sketch, "E9.42.2", {"start": v(9.8, 10.52) * mm, "mid": v(9.79, 10.2) * mm, "end": v(9.93, 9.93) * mm});
            skArc(sketch, "E9.42.3", {"start": v(10.52, 9.8) * mm, "mid": v(10.2, 9.79) * mm, "end": v(9.93, 9.93) * mm});
            skArc(sketch, "E9.42.4", {"start": v(10.78, 9.95) * mm, "mid": v(10.65, 9.87) * mm, "end": v(10.52, 9.8) * mm});
            skArc(sketch, "E9.42.5", {"start": v(10.78, 9.95) * mm, "mid": v(10.88, 9.98) * mm, "end": v(10.98, 9.93) * mm});
            skArc(sketch, "E9.43.0", {"start": v(8.45, 11.98) * mm, "mid": v(8.47, 12.09) * mm, "end": v(8.4, 12.18) * mm});
            skArc(sketch, "E9.43.1", {"start": v(8.45, 11.98) * mm, "mid": v(8.4, 11.85) * mm, "end": v(8.35, 11.7) * mm});
            skArc(sketch, "E9.43.2", {"start": v(8.35, 11.7) * mm, "mid": v(8.37, 11.4) * mm, "end": v(8.55, 11.15) * mm});
            skArc(sketch, "E9.43.3", {"start": v(9.15, 11.1) * mm, "mid": v(8.84, 11.03) * mm, "end": v(8.55, 11.15) * mm});
            skArc(sketch, "E9.43.4", {"start": v(9.39, 11.27) * mm, "mid": v(9.27, 11.17) * mm, "end": v(9.15, 11.1) * mm});
            skArc(sketch, "E9.43.5", {"start": v(9.39, 11.27) * mm, "mid": v(9.49, 11.3) * mm, "end": v(9.59, 11.27) * mm});
            skArc(sketch, "E9.44.0", {"start": v(6.82, 12.98) * mm, "mid": v(6.82, 13.1) * mm, "end": v(6.75, 13.17) * mm});
            skArc(sketch, "E9.44.1", {"start": v(6.82, 12.98) * mm, "mid": v(6.77, 12.84) * mm, "end": v(6.75, 12.7) * mm});
            skArc(sketch, "E9.44.2", {"start": v(6.75, 12.7) * mm, "mid": v(6.81, 12.4) * mm, "end": v(7.03, 12.17) * mm});
            skArc(sketch, "E9.44.3", {"start": v(7.62, 12.2) * mm, "mid": v(7.33, 12.1) * mm, "end": v(7.03, 12.17) * mm});
            skArc(sketch, "E9.44.4", {"start": v(7.83, 12.4) * mm, "mid": v(7.73, 12.29) * mm, "end": v(7.62, 12.2) * mm});
            skArc(sketch, "E9.44.5", {"start": v(7.83, 12.4) * mm, "mid": v(7.93, 12.45) * mm, "end": v(8.03, 12.43) * mm});
            skArc(sketch, "E9.45.0", {"start": v(5.06, 13.76) * mm, "mid": v(5.05, 13.87) * mm, "end": v(4.97, 13.94) * mm});
            skArc(sketch, "E9.45.1", {"start": v(5.06, 13.76) * mm, "mid": v(5.04, 13.62) * mm, "end": v(5.03, 13.47) * mm});
            skArc(sketch, "E9.45.2", {"start": v(5.03, 13.47) * mm, "mid": v(5.14, 13.17) * mm, "end": v(5.38, 12.98) * mm});
            skArc(sketch, "E9.45.3", {"start": v(5.96, 13.08) * mm, "mid": v(5.68, 12.95) * mm, "end": v(5.38, 12.98) * mm});
            skArc(sketch, "E9.45.4", {"start": v(6.15, 13.31) * mm, "mid": v(6.06, 13.2) * mm, "end": v(5.96, 13.08) * mm});
            skArc(sketch, "E9.45.5", {"start": v(6.15, 13.31) * mm, "mid": v(6.24, 13.38) * mm, "end": v(6.34, 13.37) * mm});
            skArc(sketch, "E9.46.0", {"start": v(3.23, 14.3) * mm, "mid": v(3.2, 14.41) * mm, "end": v(3.1, 14.47) * mm});
            skArc(sketch, "E9.46.1", {"start": v(3.23, 14.3) * mm, "mid": v(3.22, 14.16) * mm, "end": v(3.23, 14) * mm});
            skArc(sketch, "E9.46.2", {"start": v(3.23, 14) * mm, "mid": v(3.37, 13.73) * mm, "end": v(3.64, 13.57) * mm});
            skArc(sketch, "E9.46.3", {"start": v(4.2, 13.75) * mm, "mid": v(3.95, 13.58) * mm, "end": v(3.64, 13.57) * mm});
            skArc(sketch, "E9.46.4", {"start": v(4.36, 14) * mm, "mid": v(4.3, 13.87) * mm, "end": v(4.2, 13.75) * mm});
            skArc(sketch, "E9.46.5", {"start": v(4.36, 14) * mm, "mid": v(4.44, 14.08) * mm, "end": v(4.54, 14.09) * mm});
            skArc(sketch, "E9.47.0", {"start": v(1.33, 14.6) * mm, "mid": v(1.3, 14.7) * mm, "end": v(1.2, 14.75) * mm});
            skArc(sketch, "E9.47.1", {"start": v(1.33, 14.6) * mm, "mid": v(1.34, 14.46) * mm, "end": v(1.38, 14.31) * mm});
            skArc(sketch, "E9.47.2", {"start": v(1.38, 14.31) * mm, "mid": v(1.55, 14.05) * mm, "end": v(1.83, 13.93) * mm});
            skArc(sketch, "E9.47.3", {"start": v(2.37, 14.18) * mm, "mid": v(2.14, 13.98) * mm, "end": v(1.83, 13.93) * mm});
            skArc(sketch, "E9.47.4", {"start": v(2.5, 14.45) * mm, "mid": v(2.44, 14.31) * mm, "end": v(2.37, 14.18) * mm});
            skArc(sketch, "E9.47.5", {"start": v(2.5, 14.45) * mm, "mid": v(2.56, 14.54) * mm, "end": v(2.67, 14.56) * mm});
            skArc(sketch, "E10.trimOffspring", {"start": v(1.2, 14.75) * mm, "mid": v(0.97, 14.77) * mm, "end": v(0.74, 14.78) * mm});
            skArc(sketch, "E11.trimOffspring", {"start": v(3.1, 14.47) * mm, "mid": v(2.89, 14.52) * mm, "end": v(2.67, 14.56) * mm});
            skArc(sketch, "E12.trimOffspring", {"start": v(4.97, 13.94) * mm, "mid": v(4.76, 14.01) * mm, "end": v(4.54, 14.09) * mm});
            skArc(sketch, "E13.trimOffspring", {"start": v(6.75, 13.17) * mm, "mid": v(6.55, 13.27) * mm, "end": v(6.34, 13.37) * mm});
            skArc(sketch, "E14.trimOffspring", {"start": v(8.4, 12.18) * mm, "mid": v(8.22, 12.3) * mm, "end": v(8.03, 12.43) * mm});
            skArc(sketch, "E15.trimOffspring", {"start": v(9.93, 10.98) * mm, "mid": v(9.76, 11.13) * mm, "end": v(9.59, 11.27) * mm});
            skArc(sketch, "E16.trimOffspring", {"start": v(11.27, 9.59) * mm, "mid": v(11.13, 9.76) * mm, "end": v(10.98, 9.93) * mm});
            skArc(sketch, "E17.trimOffspring", {"start": v(12.43, 8.03) * mm, "mid": v(12.3, 8.22) * mm, "end": v(12.18, 8.4) * mm});
            skArc(sketch, "E18.trimOffspring", {"start": v(13.37, 6.34) * mm, "mid": v(13.27, 6.55) * mm, "end": v(13.17, 6.75) * mm});
            skArc(sketch, "E19.trimOffspring", {"start": v(14.09, 4.54) * mm, "mid": v(14.01, 4.76) * mm, "end": v(13.94, 4.97) * mm});
            skArc(sketch, "E20.trimOffspring", {"start": v(14.56, 2.67) * mm, "mid": v(14.52, 2.89) * mm, "end": v(14.47, 3.1) * mm});
            skArc(sketch, "E21.trimOffspring", {"start": v(14.78, 0.74) * mm, "mid": v(14.77, 0.97) * mm, "end": v(14.75, 1.2) * mm});
            skArc(sketch, "E22.trimOffspring", {"start": v(14.75, -1.2) * mm, "mid": v(14.77, -0.97) * mm, "end": v(14.78, -0.74) * mm});
            skArc(sketch, "E23.trimOffspring", {"start": v(14.47, -3.1) * mm, "mid": v(14.52, -2.89) * mm, "end": v(14.56, -2.67) * mm});
            skArc(sketch, "E24.trimOffspring", {"start": v(13.94, -4.97) * mm, "mid": v(14.01, -4.76) * mm, "end": v(14.09, -4.54) * mm});
            skArc(sketch, "E25.trimOffspring", {"start": v(13.17, -6.75) * mm, "mid": v(13.27, -6.55) * mm, "end": v(13.37, -6.34) * mm});
            skArc(sketch, "E26.trimOffspring", {"start": v(12.18, -8.4) * mm, "mid": v(12.3, -8.22) * mm, "end": v(12.43, -8.03) * mm});
            skArc(sketch, "E27.trimOffspring", {"start": v(10.98, -9.93) * mm, "mid": v(11.13, -9.76) * mm, "end": v(11.27, -9.59) * mm});
            skArc(sketch, "E28.trimOffspring", {"start": v(9.59, -11.27) * mm, "mid": v(9.76, -11.13) * mm, "end": v(9.93, -10.98) * mm});
            skArc(sketch, "E29.trimOffspring", {"start": v(8.03, -12.43) * mm, "mid": v(8.22, -12.3) * mm, "end": v(8.4, -12.18) * mm});
            skArc(sketch, "E30.trimOffspring", {"start": v(6.34, -13.37) * mm, "mid": v(6.55, -13.27) * mm, "end": v(6.75, -13.17) * mm});
            skArc(sketch, "E31.trimOffspring", {"start": v(4.54, -14.09) * mm, "mid": v(4.76, -14.01) * mm, "end": v(4.97, -13.94) * mm});
            skArc(sketch, "E32.trimOffspring", {"start": v(2.67, -14.56) * mm, "mid": v(2.89, -14.52) * mm, "end": v(3.1, -14.47) * mm});
            skArc(sketch, "E33.trimOffspring", {"start": v(0.74, -14.78) * mm, "mid": v(0.97, -14.77) * mm, "end": v(1.2, -14.75) * mm});
            skArc(sketch, "E34.trimOffspring", {"start": v(-1.2, -14.75) * mm, "mid": v(-0.97, -14.77) * mm, "end": v(-0.74, -14.78) * mm});
            skArc(sketch, "E35.trimOffspring", {"start": v(-3.1, -14.47) * mm, "mid": v(-2.89, -14.52) * mm, "end": v(-2.67, -14.56) * mm});
            skArc(sketch, "E36.trimOffspring", {"start": v(-4.97, -13.94) * mm, "mid": v(-4.76, -14.01) * mm, "end": v(-4.54, -14.09) * mm});
            skArc(sketch, "E37.trimOffspring", {"start": v(-8.4, -12.18) * mm, "mid": v(-7.4, -12.82) * mm, "end": v(-6.34, -13.37) * mm});
            skArc(sketch, "E38.trimOffspring", {"start": v(-9.93, -10.98) * mm, "mid": v(-9.76, -11.13) * mm, "end": v(-9.59, -11.27) * mm});
            skArc(sketch, "E39.trimOffspring", {"start": v(-11.27, -9.59) * mm, "mid": v(-11.13, -9.76) * mm, "end": v(-10.98, -9.93) * mm});
            skArc(sketch, "E40.trimOffspring", {"start": v(-12.43, -8.03) * mm, "mid": v(-12.3, -8.22) * mm, "end": v(-12.18, -8.4) * mm});
            skArc(sketch, "E41.trimOffspring", {"start": v(-13.37, -6.34) * mm, "mid": v(-13.27, -6.55) * mm, "end": v(-13.17, -6.75) * mm});
            skArc(sketch, "E42.trimOffspring", {"start": v(-14.09, -4.54) * mm, "mid": v(-14.01, -4.76) * mm, "end": v(-13.94, -4.97) * mm});
            skArc(sketch, "E43.trimOffspring", {"start": v(-14.56, -2.67) * mm, "mid": v(-14.52, -2.89) * mm, "end": v(-14.47, -3.1) * mm});
            skArc(sketch, "E44.trimOffspring", {"start": v(-14.78, -0.74) * mm, "mid": v(-14.77, -0.97) * mm, "end": v(-14.75, -1.2) * mm});
            skArc(sketch, "E45.trimOffspring", {"start": v(-14.75, 1.2) * mm, "mid": v(-14.77, 0.97) * mm, "end": v(-14.78, 0.74) * mm});
            skArc(sketch, "E46.trimOffspring", {"start": v(-14.47, 3.1) * mm, "mid": v(-14.52, 2.89) * mm, "end": v(-14.56, 2.67) * mm});
            skArc(sketch, "E47.trimOffspring", {"start": v(-13.94, 4.97) * mm, "mid": v(-14.01, 4.76) * mm, "end": v(-14.09, 4.54) * mm});
            skArc(sketch, "E48.trimOffspring", {"start": v(-13.17, 6.75) * mm, "mid": v(-13.27, 6.55) * mm, "end": v(-13.37, 6.34) * mm});
            skArc(sketch, "E49.trimOffspring", {"start": v(-12.18, 8.4) * mm, "mid": v(-12.3, 8.22) * mm, "end": v(-12.43, 8.03) * mm});
            skArc(sketch, "E50.trimOffspring", {"start": v(-10.98, 9.93) * mm, "mid": v(-11.13, 9.76) * mm, "end": v(-11.27, 9.59) * mm});
            skArc(sketch, "E51.trimOffspring", {"start": v(-9.59, 11.27) * mm, "mid": v(-9.76, 11.13) * mm, "end": v(-9.93, 10.98) * mm});
            skArc(sketch, "E52.trimOffspring", {"start": v(-8.03, 12.43) * mm, "mid": v(-8.22, 12.3) * mm, "end": v(-8.4, 12.18) * mm});
            skArc(sketch, "E53.trimOffspring", {"start": v(-6.34, 13.37) * mm, "mid": v(-6.55, 13.27) * mm, "end": v(-6.75, 13.17) * mm});
            skArc(sketch, "E54.trimOffspring", {"start": v(-4.54, 14.09) * mm, "mid": v(-4.76, 14.01) * mm, "end": v(-4.97, 13.94) * mm});
            skArc(sketch, "E55.trimOffspring", {"start": v(-2.67, 14.56) * mm, "mid": v(-2.89, 14.52) * mm, "end": v(-3.1, 14.47) * mm});
            skSolve(sketch);
        }
        {
            var Q0;
            {var subQ0=sQuery(id+"F0.wireOp",EDGE,"E1");var subQ38=makeQuery(id+"F0.imprint","IMPRINT",VERTEX,{"derivedFrom":subQ0});Q0=makeQuery(id+"F0.imprint","IMPRINT",FACE,{"disambiguationData":[TD([[makeQuery(id+"F0.imprint","IMPRINT",EDGE,{"disambiguationData":[TD([[subQ38,1.0]])],"derivedFrom":subQ0}),1.0]])]});}
            var Q1;
            Q1=makeQuery(id+"F0.imprint","IMPRINT",FACE,{"disambiguationData":[TD([[makeQuery(id+"F0.imprint","IMPRINT",EDGE,{"derivedFrom":sQuery(id+"F0.wireOp",EDGE,"E9.4.0")}),1.0]])]});
            var Q2;
            Q2=makeQuery(id+"F0.imprint","IMPRINT",FACE,{"disambiguationData":[TD([[makeQuery(id+"F0.imprint","IMPRINT",EDGE,{"derivedFrom":sQuery(id+"F0.wireOp",EDGE,"E9.3.0")}),1.0]])]});
            var Q3;
            Q3=makeQuery(id+"F0.imprint","IMPRINT",FACE,{"disambiguationData":[TD([[makeQuery(id+"F0.imprint","IMPRINT",EDGE,{"derivedFrom":sQuery(id+"F0.wireOp",EDGE,"E9.2.0")}),1.0]])]});
            var Q4;
            Q4=makeQuery(id+"F0.imprint","IMPRINT",FACE,{"disambiguationData":[TD([[makeQuery(id+"F0.imprint","IMPRINT",EDGE,{"derivedFrom":sQuery(id+"F0.wireOp",EDGE,"E9.1.0")}),1.0]])]});
            var Q5;
            Q5=makeQuery(id+"F0.imprint","IMPRINT",FACE,{"disambiguationData":[TD([[makeQuery(id+"F0.imprint","IMPRINT",EDGE,{"derivedFrom":sQuery(id+"F0.wireOp",EDGE,"E0")}),1.0]])]});
            var Q6;
            Q6=makeQuery(id+"F0.imprint","IMPRINT",FACE,{"disambiguationData":[TD([[makeQuery(id+"F0.imprint","IMPRINT",EDGE,{"derivedFrom":sQuery(id+"F0.wireOp",EDGE,"E6.MirrorCS")}),-1.0]])]});
            var Q7;
            Q7=makeQuery(id+"F0.imprint","IMPRINT",FACE,{"disambiguationData":[TD([[makeQuery(id+"F0.imprint","IMPRINT",EDGE,{"derivedFrom":sQuery(id+"F0.wireOp",EDGE,"E9.46.0")}),1.0]])]});
            var Q8;
            Q8=makeQuery(id+"F0.imprint","IMPRINT",FACE,{"disambiguationData":[TD([[makeQuery(id+"F0.imprint","IMPRINT",EDGE,{"derivedFrom":sQuery(id+"F0.wireOp",EDGE,"E9.45.0")}),1.0]])]});
            var Q9;
            Q9=makeQuery(id+"F0.imprint","IMPRINT",FACE,{"disambiguationData":[TD([[makeQuery(id+"F0.imprint","IMPRINT",EDGE,{"derivedFrom":sQuery(id+"F0.wireOp",EDGE,"E9.44.0")}),1.0]])]});
            var Q10;
            Q10=makeQuery(id+"F0.imprint","IMPRINT",FACE,{"disambiguationData":[TD([[makeQuery(id+"F0.imprint","IMPRINT",EDGE,{"derivedFrom":sQuery(id+"F0.wireOp",EDGE,"E9.43.0")}),1.0]])]});
            var Q11;
            Q11=makeQuery(id+"F0.imprint","IMPRINT",FACE,{"disambiguationData":[TD([[makeQuery(id+"F0.imprint","IMPRINT",EDGE,{"derivedFrom":sQuery(id+"F0.wireOp",EDGE,"E9.42.0")}),1.0]])]});
            var Q12;
            Q12=makeQuery(id+"F0.imprint","IMPRINT",FACE,{"disambiguationData":[TD([[makeQuery(id+"F0.imprint","IMPRINT",EDGE,{"derivedFrom":sQuery(id+"F0.wireOp",EDGE,"E9.41.0")}),1.0]])]});
            var Q13;
            Q13=makeQuery(id+"F0.imprint","IMPRINT",FACE,{"disambiguationData":[TD([[makeQuery(id+"F0.imprint","IMPRINT",EDGE,{"derivedFrom":sQuery(id+"F0.wireOp",EDGE,"E9.40.0")}),1.0]])]});
            var Q14;
            Q14=makeQuery(id+"F0.imprint","IMPRINT",FACE,{"disambiguationData":[TD([[makeQuery(id+"F0.imprint","IMPRINT",EDGE,{"derivedFrom":sQuery(id+"F0.wireOp",EDGE,"E9.39.0")}),1.0]])]});
            var Q15;
            Q15=makeQuery(id+"F0.imprint","IMPRINT",FACE,{"disambiguationData":[TD([[makeQuery(id+"F0.imprint","IMPRINT",EDGE,{"derivedFrom":sQuery(id+"F0.wireOp",EDGE,"E9.38.0")}),1.0]])]});
            var Q16;
            Q16=makeQuery(id+"F0.imprint","IMPRINT",FACE,{"disambiguationData":[TD([[makeQuery(id+"F0.imprint","IMPRINT",EDGE,{"derivedFrom":sQuery(id+"F0.wireOp",EDGE,"E9.37.0")}),1.0]])]});
            var Q17;
            Q17=makeQuery(id+"F0.imprint","IMPRINT",FACE,{"disambiguationData":[TD([[makeQuery(id+"F0.imprint","IMPRINT",EDGE,{"derivedFrom":sQuery(id+"F0.wireOp",EDGE,"E9.36.0")}),1.0]])]});
            var Q18;
            Q18=makeQuery(id+"F0.imprint","IMPRINT",FACE,{"disambiguationData":[TD([[makeQuery(id+"F0.imprint","IMPRINT",EDGE,{"derivedFrom":sQuery(id+"F0.wireOp",EDGE,"E9.35.0")}),1.0]])]});
            var Q19;
            Q19=makeQuery(id+"F0.imprint","IMPRINT",FACE,{"disambiguationData":[TD([[makeQuery(id+"F0.imprint","IMPRINT",EDGE,{"derivedFrom":sQuery(id+"F0.wireOp",EDGE,"E9.34.0")}),1.0]])]});
            var Q20;
            Q20=makeQuery(id+"F0.imprint","IMPRINT",FACE,{"disambiguationData":[TD([[makeQuery(id+"F0.imprint","IMPRINT",EDGE,{"derivedFrom":sQuery(id+"F0.wireOp",EDGE,"E9.33.0")}),1.0]])]});
            var Q21;
            Q21=makeQuery(id+"F0.imprint","IMPRINT",FACE,{"disambiguationData":[TD([[makeQuery(id+"F0.imprint","IMPRINT",EDGE,{"derivedFrom":sQuery(id+"F0.wireOp",EDGE,"E9.32.0")}),1.0]])]});
            var Q22;
            Q22=makeQuery(id+"F0.imprint","IMPRINT",FACE,{"disambiguationData":[TD([[makeQuery(id+"F0.imprint","IMPRINT",EDGE,{"derivedFrom":sQuery(id+"F0.wireOp",EDGE,"E9.31.0")}),1.0]])]});
            var Q23;
            Q23=makeQuery(id+"F0.imprint","IMPRINT",FACE,{"disambiguationData":[TD([[makeQuery(id+"F0.imprint","IMPRINT",EDGE,{"derivedFrom":sQuery(id+"F0.wireOp",EDGE,"E9.30.0")}),1.0]])]});
            var Q24;
            Q24=makeQuery(id+"F0.imprint","IMPRINT",FACE,{"disambiguationData":[TD([[makeQuery(id+"F0.imprint","IMPRINT",EDGE,{"derivedFrom":sQuery(id+"F0.wireOp",EDGE,"E9.29.0")}),1.0]])]});
            var Q25;
            Q25=makeQuery(id+"F0.imprint","IMPRINT",FACE,{"disambiguationData":[TD([[makeQuery(id+"F0.imprint","IMPRINT",EDGE,{"derivedFrom":sQuery(id+"F0.wireOp",EDGE,"E9.28.0")}),1.0]])]});
            var Q26;
            Q26=makeQuery(id+"F0.imprint","IMPRINT",FACE,{"disambiguationData":[TD([[makeQuery(id+"F0.imprint","IMPRINT",EDGE,{"derivedFrom":sQuery(id+"F0.wireOp",EDGE,"E9.27.0")}),1.0]])]});
            var Q27;
            Q27=makeQuery(id+"F0.imprint","IMPRINT",FACE,{"disambiguationData":[TD([[makeQuery(id+"F0.imprint","IMPRINT",EDGE,{"derivedFrom":sQuery(id+"F0.wireOp",EDGE,"E9.26.0")}),1.0]])]});
            var Q28;
            Q28=makeQuery(id+"F0.imprint","IMPRINT",FACE,{"disambiguationData":[TD([[makeQuery(id+"F0.imprint","IMPRINT",EDGE,{"derivedFrom":sQuery(id+"F0.wireOp",EDGE,"E9.25.0")}),1.0]])]});
            var Q29;
            Q29=makeQuery(id+"F0.imprint","IMPRINT",FACE,{"disambiguationData":[TD([[makeQuery(id+"F0.imprint","IMPRINT",EDGE,{"derivedFrom":sQuery(id+"F0.wireOp",EDGE,"E9.24.0")}),1.0]])]});
            var Q30;
            Q30=makeQuery(id+"F0.imprint","IMPRINT",FACE,{"disambiguationData":[TD([[makeQuery(id+"F0.imprint","IMPRINT",EDGE,{"derivedFrom":sQuery(id+"F0.wireOp",EDGE,"E9.23.0")}),1.0]])]});
            var Q31;
            Q31=makeQuery(id+"F0.imprint","IMPRINT",FACE,{"disambiguationData":[TD([[makeQuery(id+"F0.imprint","IMPRINT",EDGE,{"derivedFrom":sQuery(id+"F0.wireOp",EDGE,"E9.22.0")}),1.0]])]});
            var Q32;
            Q32=makeQuery(id+"F0.imprint","IMPRINT",FACE,{"disambiguationData":[TD([[makeQuery(id+"F0.imprint","IMPRINT",EDGE,{"derivedFrom":sQuery(id+"F0.wireOp",EDGE,"E9.21.0")}),1.0]])]});
            var Q33;
            {var subQ1=sQuery(id+"F0.wireOp",EDGE,"E9.20.0");Q33=makeQuery(id+"F0.imprint","IMPRINT",FACE,{"disambiguationData":[TD([[makeQuery(id+"F0.imprint","IMPRINT",EDGE,{"derivedFrom":subQ1}),1.0]])]});}
            var Q34;
            {var subQ3=sQuery(id+"F0.wireOp",EDGE,"E9.19.0");Q34=makeQuery(id+"F0.imprint","IMPRINT",FACE,{"disambiguationData":[TD([[makeQuery(id+"F0.imprint","IMPRINT",EDGE,{"derivedFrom":subQ3}),1.0]])]});}
            var Q35;
            Q35=makeQuery(id+"F0.imprint","IMPRINT",FACE,{"disambiguationData":[TD([[makeQuery(id+"F0.imprint","IMPRINT",EDGE,{"derivedFrom":sQuery(id+"F0.wireOp",EDGE,"E9.18.0")}),1.0]])]});
            var Q36;
            Q36=makeQuery(id+"F0.imprint","IMPRINT",FACE,{"disambiguationData":[TD([[makeQuery(id+"F0.imprint","IMPRINT",EDGE,{"derivedFrom":sQuery(id+"F0.wireOp",EDGE,"E9.17.0")}),1.0]])]});
            var Q37;
            Q37=makeQuery(id+"F0.imprint","IMPRINT",FACE,{"disambiguationData":[TD([[makeQuery(id+"F0.imprint","IMPRINT",EDGE,{"derivedFrom":sQuery(id+"F0.wireOp",EDGE,"E9.16.0")}),1.0]])]});
            var Q38;
            Q38=makeQuery(id+"F0.imprint","IMPRINT",FACE,{"disambiguationData":[TD([[makeQuery(id+"F0.imprint","IMPRINT",EDGE,{"derivedFrom":sQuery(id+"F0.wireOp",EDGE,"E9.15.0")}),1.0]])]});
            var Q39;
            Q39=makeQuery(id+"F0.imprint","IMPRINT",FACE,{"disambiguationData":[TD([[makeQuery(id+"F0.imprint","IMPRINT",EDGE,{"derivedFrom":sQuery(id+"F0.wireOp",EDGE,"E9.14.0")}),1.0]])]});
            var Q40;
            Q40=makeQuery(id+"F0.imprint","IMPRINT",FACE,{"disambiguationData":[TD([[makeQuery(id+"F0.imprint","IMPRINT",EDGE,{"derivedFrom":sQuery(id+"F0.wireOp",EDGE,"E9.13.0")}),1.0]])]});
            var Q41;
            Q41=makeQuery(id+"F0.imprint","IMPRINT",FACE,{"disambiguationData":[TD([[makeQuery(id+"F0.imprint","IMPRINT",EDGE,{"derivedFrom":sQuery(id+"F0.wireOp",EDGE,"E9.12.0")}),1.0]])]});
            var Q42;
            Q42=makeQuery(id+"F0.imprint","IMPRINT",FACE,{"disambiguationData":[TD([[makeQuery(id+"F0.imprint","IMPRINT",EDGE,{"derivedFrom":sQuery(id+"F0.wireOp",EDGE,"E9.11.0")}),1.0]])]});
            var Q43;
            Q43=makeQuery(id+"F0.imprint","IMPRINT",FACE,{"disambiguationData":[TD([[makeQuery(id+"F0.imprint","IMPRINT",EDGE,{"derivedFrom":sQuery(id+"F0.wireOp",EDGE,"E9.10.0")}),1.0]])]});
            var Q44;
            Q44=makeQuery(id+"F0.imprint","IMPRINT",FACE,{"disambiguationData":[TD([[makeQuery(id+"F0.imprint","IMPRINT",EDGE,{"derivedFrom":sQuery(id+"F0.wireOp",EDGE,"E9.7.0")}),1.0]])]});
            var Q45;
            Q45=makeQuery(id+"F0.imprint","IMPRINT",FACE,{"disambiguationData":[TD([[makeQuery(id+"F0.imprint","IMPRINT",EDGE,{"derivedFrom":sQuery(id+"F0.wireOp",EDGE,"E9.6.0")}),1.0]])]});
            var Q46;
            Q46=makeQuery(id+"F0.imprint","IMPRINT",FACE,{"disambiguationData":[TD([[makeQuery(id+"F0.imprint","IMPRINT",EDGE,{"derivedFrom":sQuery(id+"F0.wireOp",EDGE,"E9.5.0")}),1.0]])]});
            var Q47;
            Q47=makeQuery(id+"F0.imprint","IMPRINT",FACE,{"disambiguationData":[TD([[makeQuery(id+"F0.imprint","IMPRINT",EDGE,{"derivedFrom":sQuery(id+"F0.wireOp",EDGE,"E9.8.0")}),1.0]])]});
            var Q48;
            Q48=makeQuery(id+"F0.imprint","IMPRINT",FACE,{"disambiguationData":[TD([[makeQuery(id+"F0.imprint","IMPRINT",EDGE,{"derivedFrom":sQuery(id+"F0.wireOp",EDGE,"E9.9.0")}),1.0]])]});
            extrude(context, id + "F1", {"entities" : qUnion([Q0, Q1, Q2, Q3, Q4, Q5, Q6, Q7, Q8, Q9, Q10, Q11, Q12, Q13, Q14, Q15, Q16, Q17, Q18, Q19, Q20, Q21, Q22, Q23, Q24, Q25, Q26, Q27, Q28, Q29, Q30, Q31, Q32, Q33, Q34, Q35, Q36, Q37, Q38, Q39, Q40, Q41, Q42, Q43, Q44, Q45, Q46, Q47, Q48]), "depth" : 6.5 * mm, "offsetDistance" : 25 * mm});
        }
        {
            var Q0;
            Q0=makeQuery(id+"F1.opExtrude","CAP_FACE",FACE,{"disambiguationData":[OSD([sQuery(id+"F0.wireOp",EDGE,"E0"),sQuery(id+"F0.wireOp",EDGE,"E2"),sQuery(id+"F0.wireOp",EDGE,"E4"),sQuery(id+"F0.wireOp",EDGE,"E5"),sQuery(id+"F0.wireOp",EDGE,"E6.MirrorCS"),sQuery(id+"F0.wireOp",EDGE,"E7.MirrorCS"),sQuery(id+"F0.wireOp",EDGE,"E8.MirrorCS"),sQuery(id+"F0.wireOp",EDGE,"E9.1.0"),sQuery(id+"F0.wireOp",EDGE,"E9.1.1"),sQuery(id+"F0.wireOp",EDGE,"E9.1.2"),sQuery(id+"F0.wireOp",EDGE,"E9.1.3"),sQuery(id+"F0.wireOp",EDGE,"E9.1.4"),sQuery(id+"F0.wireOp",EDGE,"E9.1.5"),sQuery(id+"F0.wireOp",EDGE,"E9.2.0"),sQuery(id+"F0.wireOp",EDGE,"E9.2.1"),sQuery(id+"F0.wireOp",EDGE,"E9.2.2"),sQuery(id+"F0.wireOp",EDGE,"E9.2.3"),sQuery(id+"F0.wireOp",EDGE,"E9.2.4"),sQuery(id+"F0.wireOp",EDGE,"E9.2.5"),sQuery(id+"F0.wireOp",EDGE,"E9.3.0"),sQuery(id+"F0.wireOp",EDGE,"E9.3.1"),sQuery(id+"F0.wireOp",EDGE,"E9.3.2"),sQuery(id+"F0.wireOp",EDGE,"E9.3.3"),sQuery(id+"F0.wireOp",EDGE,"E9.3.4"),sQuery(id+"F0.wireOp",EDGE,"E9.3.5"),sQuery(id+"F0.wireOp",EDGE,"E9.4.0"),sQuery(id+"F0.wireOp",EDGE,"E9.4.1"),sQuery(id+"F0.wireOp",EDGE,"E9.4.2"),sQuery(id+"F0.wireOp",EDGE,"E9.4.3"),sQuery(id+"F0.wireOp",EDGE,"E9.4.4"),sQuery(id+"F0.wireOp",EDGE,"E9.4.5"),sQuery(id+"F0.wireOp",EDGE,"E9.5.0"),sQuery(id+"F0.wireOp",EDGE,"E9.5.1"),sQuery(id+"F0.wireOp",EDGE,"E9.5.2"),sQuery(id+"F0.wireOp",EDGE,"E9.5.3"),sQuery(id+"F0.wireOp",EDGE,"E9.5.4"),sQuery(id+"F0.wireOp",EDGE,"E9.5.5"),sQuery(id+"F0.wireOp",EDGE,"E9.6.0"),sQuery(id+"F0.wireOp",EDGE,"E9.6.1"),sQuery(id+"F0.wireOp",EDGE,"E9.6.2"),sQuery(id+"F0.wireOp",EDGE,"E9.6.3"),sQuery(id+"F0.wireOp",EDGE,"E9.6.4"),sQuery(id+"F0.wireOp",EDGE,"E9.6.5"),sQuery(id+"F0.wireOp",EDGE,"E9.7.0"),sQuery(id+"F0.wireOp",EDGE,"E9.7.1"),sQuery(id+"F0.wireOp",EDGE,"E9.7.2"),sQuery(id+"F0.wireOp",EDGE,"E9.7.3"),sQuery(id+"F0.wireOp",EDGE,"E9.7.4"),sQuery(id+"F0.wireOp",EDGE,"E9.7.5"),sQuery(id+"F0.wireOp",EDGE,"E9.8.0"),sQuery(id+"F0.wireOp",EDGE,"E9.8.1"),sQuery(id+"F0.wireOp",EDGE,"E9.8.2"),sQuery(id+"F0.wireOp",EDGE,"E9.8.3"),sQuery(id+"F0.wireOp",EDGE,"E9.8.4"),sQuery(id+"F0.wireOp",EDGE,"E9.8.5"),sQuery(id+"F0.wireOp",EDGE,"E9.9.0"),sQuery(id+"F0.wireOp",EDGE,"E9.9.1"),sQuery(id+"F0.wireOp",EDGE,"E9.9.2"),sQuery(id+"F0.wireOp",EDGE,"E9.9.3"),sQuery(id+"F0.wireOp",EDGE,"E9.9.4"),sQuery(id+"F0.wireOp",EDGE,"E9.9.5"),sQuery(id+"F0.wireOp",EDGE,"E9.10.0"),sQuery(id+"F0.wireOp",EDGE,"E9.10.1"),sQuery(id+"F0.wireOp",EDGE,"E9.10.2"),sQuery(id+"F0.wireOp",EDGE,"E9.10.3"),sQuery(id+"F0.wireOp",EDGE,"E9.10.4"),sQuery(id+"F0.wireOp",EDGE,"E9.10.5"),sQuery(id+"F0.wireOp",EDGE,"E9.11.0"),sQuery(id+"F0.wireOp",EDGE,"E9.11.1"),sQuery(id+"F0.wireOp",EDGE,"E9.11.2"),sQuery(id+"F0.wireOp",EDGE,"E9.11.3"),sQuery(id+"F0.wireOp",EDGE,"E9.11.4"),sQuery(id+"F0.wireOp",EDGE,"E9.11.5"),sQuery(id+"F0.wireOp",EDGE,"E9.12.0"),sQuery(id+"F0.wireOp",EDGE,"E9.12.1"),sQuery(id+"F0.wireOp",EDGE,"E9.12.2"),sQuery(id+"F0.wireOp",EDGE,"E9.12.3"),sQuery(id+"F0.wireOp",EDGE,"E9.12.4"),sQuery(id+"F0.wireOp",EDGE,"E9.12.5"),sQuery(id+"F0.wireOp",EDGE,"E9.13.0"),sQuery(id+"F0.wireOp",EDGE,"E9.13.1"),sQuery(id+"F0.wireOp",EDGE,"E9.13.2"),sQuery(id+"F0.wireOp",EDGE,"E9.13.3"),sQuery(id+"F0.wireOp",EDGE,"E9.13.4"),sQuery(id+"F0.wireOp",EDGE,"E9.13.5"),sQuery(id+"F0.wireOp",EDGE,"E9.14.0"),sQuery(id+"F0.wireOp",EDGE,"E9.14.1"),sQuery(id+"F0.wireOp",EDGE,"E9.14.2"),sQuery(id+"F0.wireOp",EDGE,"E9.14.3"),sQuery(id+"F0.wireOp",EDGE,"E9.14.4"),sQuery(id+"F0.wireOp",EDGE,"E9.14.5"),sQuery(id+"F0.wireOp",EDGE,"E9.15.0"),sQuery(id+"F0.wireOp",EDGE,"E9.15.1"),sQuery(id+"F0.wireOp",EDGE,"E9.15.2"),sQuery(id+"F0.wireOp",EDGE,"E9.15.3"),sQuery(id+"F0.wireOp",EDGE,"E9.15.4"),sQuery(id+"F0.wireOp",EDGE,"E9.15.5"),sQuery(id+"F0.wireOp",EDGE,"E9.16.0"),sQuery(id+"F0.wireOp",EDGE,"E9.16.1"),sQuery(id+"F0.wireOp",EDGE,"E9.16.2"),sQuery(id+"F0.wireOp",EDGE,"E9.16.3"),sQuery(id+"F0.wireOp",EDGE,"E9.16.4"),sQuery(id+"F0.wireOp",EDGE,"E9.16.5"),sQuery(id+"F0.wireOp",EDGE,"E9.17.0"),sQuery(id+"F0.wireOp",EDGE,"E9.17.1"),sQuery(id+"F0.wireOp",EDGE,"E9.17.2"),sQuery(id+"F0.wireOp",EDGE,"E9.17.3"),sQuery(id+"F0.wireOp",EDGE,"E9.17.4"),sQuery(id+"F0.wireOp",EDGE,"E9.17.5"),sQuery(id+"F0.wireOp",EDGE,"E9.18.0"),sQuery(id+"F0.wireOp",EDGE,"E9.18.1"),sQuery(id+"F0.wireOp",EDGE,"E9.18.2"),sQuery(id+"F0.wireOp",EDGE,"E9.18.3"),sQuery(id+"F0.wireOp",EDGE,"E9.18.4"),sQuery(id+"F0.wireOp",EDGE,"E9.18.5"),sQuery(id+"F0.wireOp",EDGE,"E9.19.0"),sQuery(id+"F0.wireOp",EDGE,"E9.19.1"),sQuery(id+"F0.wireOp",EDGE,"E9.19.2"),sQuery(id+"F0.wireOp",EDGE,"E9.19.3"),sQuery(id+"F0.wireOp",EDGE,"E9.19.4"),sQuery(id+"F0.wireOp",EDGE,"E9.19.5"),sQuery(id+"F0.wireOp",EDGE,"E9.20.0"),sQuery(id+"F0.wireOp",EDGE,"E9.20.1"),sQuery(id+"F0.wireOp",EDGE,"E9.20.2"),sQuery(id+"F0.wireOp",EDGE,"E9.20.3"),sQuery(id+"F0.wireOp",EDGE,"E9.20.4"),sQuery(id+"F0.wireOp",EDGE,"E9.20.5"),sQuery(id+"F0.wireOp",EDGE,"E9.21.0"),sQuery(id+"F0.wireOp",EDGE,"E9.21.1"),sQuery(id+"F0.wireOp",EDGE,"E9.21.2"),sQuery(id+"F0.wireOp",EDGE,"E9.21.3"),sQuery(id+"F0.wireOp",EDGE,"E9.21.4"),sQuery(id+"F0.wireOp",EDGE,"E9.21.5"),sQuery(id+"F0.wireOp",EDGE,"E9.22.0"),sQuery(id+"F0.wireOp",EDGE,"E9.22.1"),sQuery(id+"F0.wireOp",EDGE,"E9.22.2"),sQuery(id+"F0.wireOp",EDGE,"E9.22.3"),sQuery(id+"F0.wireOp",EDGE,"E9.22.4"),sQuery(id+"F0.wireOp",EDGE,"E9.22.5"),sQuery(id+"F0.wireOp",EDGE,"E9.23.0"),sQuery(id+"F0.wireOp",EDGE,"E9.23.1"),sQuery(id+"F0.wireOp",EDGE,"E9.23.2"),sQuery(id+"F0.wireOp",EDGE,"E9.23.3"),sQuery(id+"F0.wireOp",EDGE,"E9.23.4"),sQuery(id+"F0.wireOp",EDGE,"E9.23.5"),sQuery(id+"F0.wireOp",EDGE,"E9.24.0"),sQuery(id+"F0.wireOp",EDGE,"E9.24.1"),sQuery(id+"F0.wireOp",EDGE,"E9.24.2"),sQuery(id+"F0.wireOp",EDGE,"E9.24.3"),sQuery(id+"F0.wireOp",EDGE,"E9.24.4"),sQuery(id+"F0.wireOp",EDGE,"E9.24.5"),sQuery(id+"F0.wireOp",EDGE,"E9.25.0"),sQuery(id+"F0.wireOp",EDGE,"E9.25.1"),sQuery(id+"F0.wireOp",EDGE,"E9.25.2"),sQuery(id+"F0.wireOp",EDGE,"E9.25.3"),sQuery(id+"F0.wireOp",EDGE,"E9.25.4"),sQuery(id+"F0.wireOp",EDGE,"E9.25.5"),sQuery(id+"F0.wireOp",EDGE,"E9.26.0"),sQuery(id+"F0.wireOp",EDGE,"E9.26.1"),sQuery(id+"F0.wireOp",EDGE,"E9.26.2"),sQuery(id+"F0.wireOp",EDGE,"E9.26.3"),sQuery(id+"F0.wireOp",EDGE,"E9.26.4"),sQuery(id+"F0.wireOp",EDGE,"E9.26.5"),sQuery(id+"F0.wireOp",EDGE,"E9.27.0"),sQuery(id+"F0.wireOp",EDGE,"E9.27.1"),sQuery(id+"F0.wireOp",EDGE,"E9.27.2"),sQuery(id+"F0.wireOp",EDGE,"E9.27.3"),sQuery(id+"F0.wireOp",EDGE,"E9.27.4"),sQuery(id+"F0.wireOp",EDGE,"E9.27.5"),sQuery(id+"F0.wireOp",EDGE,"E9.28.0"),sQuery(id+"F0.wireOp",EDGE,"E9.28.1"),sQuery(id+"F0.wireOp",EDGE,"E9.28.2"),sQuery(id+"F0.wireOp",EDGE,"E9.28.3"),sQuery(id+"F0.wireOp",EDGE,"E9.28.4"),sQuery(id+"F0.wireOp",EDGE,"E9.28.5"),sQuery(id+"F0.wireOp",EDGE,"E9.29.0"),sQuery(id+"F0.wireOp",EDGE,"E9.29.1"),sQuery(id+"F0.wireOp",EDGE,"E9.29.2"),sQuery(id+"F0.wireOp",EDGE,"E9.29.3"),sQuery(id+"F0.wireOp",EDGE,"E9.29.4"),sQuery(id+"F0.wireOp",EDGE,"E9.29.5"),sQuery(id+"F0.wireOp",EDGE,"E9.30.0"),sQuery(id+"F0.wireOp",EDGE,"E9.30.1"),sQuery(id+"F0.wireOp",EDGE,"E9.30.2"),sQuery(id+"F0.wireOp",EDGE,"E9.30.3"),sQuery(id+"F0.wireOp",EDGE,"E9.30.4"),sQuery(id+"F0.wireOp",EDGE,"E9.30.5"),sQuery(id+"F0.wireOp",EDGE,"E9.31.0"),sQuery(id+"F0.wireOp",EDGE,"E9.31.1"),sQuery(id+"F0.wireOp",EDGE,"E9.31.2"),sQuery(id+"F0.wireOp",EDGE,"E9.31.3"),sQuery(id+"F0.wireOp",EDGE,"E9.31.4"),sQuery(id+"F0.wireOp",EDGE,"E9.31.5"),sQuery(id+"F0.wireOp",EDGE,"E9.32.0"),sQuery(id+"F0.wireOp",EDGE,"E9.32.1"),sQuery(id+"F0.wireOp",EDGE,"E9.32.2"),sQuery(id+"F0.wireOp",EDGE,"E9.32.3"),sQuery(id+"F0.wireOp",EDGE,"E9.32.4"),sQuery(id+"F0.wireOp",EDGE,"E9.32.5"),sQuery(id+"F0.wireOp",EDGE,"E9.33.0"),sQuery(id+"F0.wireOp",EDGE,"E9.33.1"),sQuery(id+"F0.wireOp",EDGE,"E9.33.2"),sQuery(id+"F0.wireOp",EDGE,"E9.33.3"),sQuery(id+"F0.wireOp",EDGE,"E9.33.4"),sQuery(id+"F0.wireOp",EDGE,"E9.33.5"),sQuery(id+"F0.wireOp",EDGE,"E9.34.0"),sQuery(id+"F0.wireOp",EDGE,"E9.34.1"),sQuery(id+"F0.wireOp",EDGE,"E9.34.2"),sQuery(id+"F0.wireOp",EDGE,"E9.34.3"),sQuery(id+"F0.wireOp",EDGE,"E9.34.4"),sQuery(id+"F0.wireOp",EDGE,"E9.34.5"),sQuery(id+"F0.wireOp",EDGE,"E9.35.0"),sQuery(id+"F0.wireOp",EDGE,"E9.35.1"),sQuery(id+"F0.wireOp",EDGE,"E9.35.2"),sQuery(id+"F0.wireOp",EDGE,"E9.35.3"),sQuery(id+"F0.wireOp",EDGE,"E9.35.4"),sQuery(id+"F0.wireOp",EDGE,"E9.35.5"),sQuery(id+"F0.wireOp",EDGE,"E9.36.0"),sQuery(id+"F0.wireOp",EDGE,"E9.36.1"),sQuery(id+"F0.wireOp",EDGE,"E9.36.2"),sQuery(id+"F0.wireOp",EDGE,"E9.36.3"),sQuery(id+"F0.wireOp",EDGE,"E9.36.4"),sQuery(id+"F0.wireOp",EDGE,"E9.36.5"),sQuery(id+"F0.wireOp",EDGE,"E9.37.0"),sQuery(id+"F0.wireOp",EDGE,"E9.37.1"),sQuery(id+"F0.wireOp",EDGE,"E9.37.2"),sQuery(id+"F0.wireOp",EDGE,"E9.37.3"),sQuery(id+"F0.wireOp",EDGE,"E9.37.4"),sQuery(id+"F0.wireOp",EDGE,"E9.37.5"),sQuery(id+"F0.wireOp",EDGE,"E9.38.0"),sQuery(id+"F0.wireOp",EDGE,"E9.38.1"),sQuery(id+"F0.wireOp",EDGE,"E9.38.2"),sQuery(id+"F0.wireOp",EDGE,"E9.38.3"),sQuery(id+"F0.wireOp",EDGE,"E9.38.4"),sQuery(id+"F0.wireOp",EDGE,"E9.38.5"),sQuery(id+"F0.wireOp",EDGE,"E9.39.0"),sQuery(id+"F0.wireOp",EDGE,"E9.39.1"),sQuery(id+"F0.wireOp",EDGE,"E9.39.2"),sQuery(id+"F0.wireOp",EDGE,"E9.39.3"),sQuery(id+"F0.wireOp",EDGE,"E9.39.4"),sQuery(id+"F0.wireOp",EDGE,"E9.39.5"),sQuery(id+"F0.wireOp",EDGE,"E9.40.0"),sQuery(id+"F0.wireOp",EDGE,"E9.40.1"),sQuery(id+"F0.wireOp",EDGE,"E9.40.2"),sQuery(id+"F0.wireOp",EDGE,"E9.40.3"),sQuery(id+"F0.wireOp",EDGE,"E9.40.4"),sQuery(id+"F0.wireOp",EDGE,"E9.40.5"),sQuery(id+"F0.wireOp",EDGE,"E9.41.0"),sQuery(id+"F0.wireOp",EDGE,"E9.41.1"),sQuery(id+"F0.wireOp",EDGE,"E9.41.2"),sQuery(id+"F0.wireOp",EDGE,"E9.41.3"),sQuery(id+"F0.wireOp",EDGE,"E9.41.4"),sQuery(id+"F0.wireOp",EDGE,"E9.41.5"),sQuery(id+"F0.wireOp",EDGE,"E9.42.0"),sQuery(id+"F0.wireOp",EDGE,"E9.42.1"),sQuery(id+"F0.wireOp",EDGE,"E9.42.2"),sQuery(id+"F0.wireOp",EDGE,"E9.42.3"),sQuery(id+"F0.wireOp",EDGE,"E9.42.4"),sQuery(id+"F0.wireOp",EDGE,"E9.42.5"),sQuery(id+"F0.wireOp",EDGE,"E9.43.0"),sQuery(id+"F0.wireOp",EDGE,"E9.43.1"),sQuery(id+"F0.wireOp",EDGE,"E9.43.2"),sQuery(id+"F0.wireOp",EDGE,"E9.43.3"),sQuery(id+"F0.wireOp",EDGE,"E9.43.4"),sQuery(id+"F0.wireOp",EDGE,"E9.43.5"),sQuery(id+"F0.wireOp",EDGE,"E9.44.0"),sQuery(id+"F0.wireOp",EDGE,"E9.44.1"),sQuery(id+"F0.wireOp",EDGE,"E9.44.2"),sQuery(id+"F0.wireOp",EDGE,"E9.44.3"),sQuery(id+"F0.wireOp",EDGE,"E9.44.4"),sQuery(id+"F0.wireOp",EDGE,"E9.44.5"),sQuery(id+"F0.wireOp",EDGE,"E9.45.0"),sQuery(id+"F0.wireOp",EDGE,"E9.45.1"),sQuery(id+"F0.wireOp",EDGE,"E9.45.2"),sQuery(id+"F0.wireOp",EDGE,"E9.45.3"),sQuery(id+"F0.wireOp",EDGE,"E9.45.4"),sQuery(id+"F0.wireOp",EDGE,"E9.45.5"),sQuery(id+"F0.wireOp",EDGE,"E9.46.0"),sQuery(id+"F0.wireOp",EDGE,"E9.46.1"),sQuery(id+"F0.wireOp",EDGE,"E9.46.2"),sQuery(id+"F0.wireOp",EDGE,"E9.46.3"),sQuery(id+"F0.wireOp",EDGE,"E9.46.4"),sQuery(id+"F0.wireOp",EDGE,"E9.46.5"),sQuery(id+"F0.wireOp",EDGE,"E9.47.0"),sQuery(id+"F0.wireOp",EDGE,"E9.47.1"),sQuery(id+"F0.wireOp",EDGE,"E9.47.2"),sQuery(id+"F0.wireOp",EDGE,"E9.47.3"),sQuery(id+"F0.wireOp",EDGE,"E9.47.4"),sQuery(id+"F0.wireOp",EDGE,"E9.47.5"),sQuery(id+"F0.wireOp",EDGE,"E10.trimOffspring"),sQuery(id+"F0.wireOp",EDGE,"E11.trimOffspring"),sQuery(id+"F0.wireOp",EDGE,"E12.trimOffspring"),sQuery(id+"F0.wireOp",EDGE,"E13.trimOffspring"),sQuery(id+"F0.wireOp",EDGE,"E14.trimOffspring"),sQuery(id+"F0.wireOp",EDGE,"E15.trimOffspring"),sQuery(id+"F0.wireOp",EDGE,"E16.trimOffspring"),sQuery(id+"F0.wireOp",EDGE,"E17.trimOffspring"),sQuery(id+"F0.wireOp",EDGE,"E18.trimOffspring"),sQuery(id+"F0.wireOp",EDGE,"E19.trimOffspring"),sQuery(id+"F0.wireOp",EDGE,"E20.trimOffspring"),sQuery(id+"F0.wireOp",EDGE,"E21.trimOffspring"),sQuery(id+"F0.wireOp",EDGE,"E22.trimOffspring"),sQuery(id+"F0.wireOp",EDGE,"E23.trimOffspring"),sQuery(id+"F0.wireOp",EDGE,"E24.trimOffspring"),sQuery(id+"F0.wireOp",EDGE,"E25.trimOffspring"),sQuery(id+"F0.wireOp",EDGE,"E26.trimOffspring"),sQuery(id+"F0.wireOp",EDGE,"E27.trimOffspring"),sQuery(id+"F0.wireOp",EDGE,"E28.trimOffspring"),sQuery(id+"F0.wireOp",EDGE,"E29.trimOffspring"),sQuery(id+"F0.wireOp",EDGE,"E30.trimOffspring"),sQuery(id+"F0.wireOp",EDGE,"E31.trimOffspring"),sQuery(id+"F0.wireOp",EDGE,"E32.trimOffspring"),sQuery(id+"F0.wireOp",EDGE,"E33.trimOffspring"),sQuery(id+"F0.wireOp",EDGE,"E34.trimOffspring"),sQuery(id+"F0.wireOp",EDGE,"E35.trimOffspring"),sQuery(id+"F0.wireOp",EDGE,"E36.trimOffspring"),sQuery(id+"F0.wireOp",EDGE,"E37.trimOffspring"),sQuery(id+"F0.wireOp",EDGE,"E38.trimOffspring"),sQuery(id+"F0.wireOp",EDGE,"E39.trimOffspring"),sQuery(id+"F0.wireOp",EDGE,"E40.trimOffspring"),sQuery(id+"F0.wireOp",EDGE,"E41.trimOffspring"),sQuery(id+"F0.wireOp",EDGE,"E42.trimOffspring"),sQuery(id+"F0.wireOp",EDGE,"E43.trimOffspring"),sQuery(id+"F0.wireOp",EDGE,"E44.trimOffspring"),sQuery(id+"F0.wireOp",EDGE,"E45.trimOffspring"),sQuery(id+"F0.wireOp",EDGE,"E46.trimOffspring"),sQuery(id+"F0.wireOp",EDGE,"E47.trimOffspring"),sQuery(id+"F0.wireOp",EDGE,"E48.trimOffspring"),sQuery(id+"F0.wireOp",EDGE,"E49.trimOffspring"),sQuery(id+"F0.wireOp",EDGE,"E50.trimOffspring"),sQuery(id+"F0.wireOp",EDGE,"E51.trimOffspring"),sQuery(id+"F0.wireOp",EDGE,"E52.trimOffspring"),sQuery(id+"F0.wireOp",EDGE,"E53.trimOffspring"),sQuery(id+"F0.wireOp",EDGE,"E54.trimOffspring"),sQuery(id+"F0.wireOp",EDGE,"E55.trimOffspring")])],"isStart":false});
            var sketch = newSketch(context, id + "F2", { "sketchPlane" : qUnion([Q0])});
            skCircle(sketch, "E56", {"center": v(0, 0) * mm, "radius": 15.5 * mm});
            skSolve(sketch);
        }
        {
            var Q0;
            Q0=makeQuery(id+"F2.imprint","IMPRINT",FACE,{"disambiguationData":[TD([[makeQuery(id+"F2.imprint","IMPRINT",EDGE,{"derivedFrom":sQuery(id+"F2.wireOp",EDGE,"E56")}),1.0]])]});
            var Q1;
            Q1=makeQuery(id+"F2.imprint","IMPRINT",FACE,{"disambiguationData":[TD([[makeQuery(id+"F2.imprint","IMPRINT",EDGE,{"derivedFrom":makeQuery(id+"F1.opExtrude","CAP_EDGE",EDGE,{"disambiguationData":[OSD([sQuery(id+"F0.wireOp",EDGE,"E0")])],"isStart":false})}),1.0]])]});
            extrude(context, id + "F3", {"entities" : qUnion([Q0, Q1]), "operationType" : NewBodyOperationType.ADD, "depth" : .5 * mm, "offsetDistance" : 25 * mm});
        }
        {
            var Q0;
            Q0=makeQuery(id+"F1.opExtrude","CAP_FACE",FACE,{"disambiguationData":[OSD([sQuery(id+"F0.wireOp",EDGE,"E0"),sQuery(id+"F0.wireOp",EDGE,"E2"),sQuery(id+"F0.wireOp",EDGE,"E4"),sQuery(id+"F0.wireOp",EDGE,"E5"),sQuery(id+"F0.wireOp",EDGE,"E6.MirrorCS"),sQuery(id+"F0.wireOp",EDGE,"E7.MirrorCS"),sQuery(id+"F0.wireOp",EDGE,"E8.MirrorCS"),sQuery(id+"F0.wireOp",EDGE,"E9.1.0"),sQuery(id+"F0.wireOp",EDGE,"E9.1.1"),sQuery(id+"F0.wireOp",EDGE,"E9.1.2"),sQuery(id+"F0.wireOp",EDGE,"E9.1.3"),sQuery(id+"F0.wireOp",EDGE,"E9.1.4"),sQuery(id+"F0.wireOp",EDGE,"E9.1.5"),sQuery(id+"F0.wireOp",EDGE,"E9.2.0"),sQuery(id+"F0.wireOp",EDGE,"E9.2.1"),sQuery(id+"F0.wireOp",EDGE,"E9.2.2"),sQuery(id+"F0.wireOp",EDGE,"E9.2.3"),sQuery(id+"F0.wireOp",EDGE,"E9.2.4"),sQuery(id+"F0.wireOp",EDGE,"E9.2.5"),sQuery(id+"F0.wireOp",EDGE,"E9.3.0"),sQuery(id+"F0.wireOp",EDGE,"E9.3.1"),sQuery(id+"F0.wireOp",EDGE,"E9.3.2"),sQuery(id+"F0.wireOp",EDGE,"E9.3.3"),sQuery(id+"F0.wireOp",EDGE,"E9.3.4"),sQuery(id+"F0.wireOp",EDGE,"E9.3.5"),sQuery(id+"F0.wireOp",EDGE,"E9.4.0"),sQuery(id+"F0.wireOp",EDGE,"E9.4.1"),sQuery(id+"F0.wireOp",EDGE,"E9.4.2"),sQuery(id+"F0.wireOp",EDGE,"E9.4.3"),sQuery(id+"F0.wireOp",EDGE,"E9.4.4"),sQuery(id+"F0.wireOp",EDGE,"E9.4.5"),sQuery(id+"F0.wireOp",EDGE,"E9.5.0"),sQuery(id+"F0.wireOp",EDGE,"E9.5.1"),sQuery(id+"F0.wireOp",EDGE,"E9.5.2"),sQuery(id+"F0.wireOp",EDGE,"E9.5.3"),sQuery(id+"F0.wireOp",EDGE,"E9.5.4"),sQuery(id+"F0.wireOp",EDGE,"E9.5.5"),sQuery(id+"F0.wireOp",EDGE,"E9.6.0"),sQuery(id+"F0.wireOp",EDGE,"E9.6.1"),sQuery(id+"F0.wireOp",EDGE,"E9.6.2"),sQuery(id+"F0.wireOp",EDGE,"E9.6.3"),sQuery(id+"F0.wireOp",EDGE,"E9.6.4"),sQuery(id+"F0.wireOp",EDGE,"E9.6.5"),sQuery(id+"F0.wireOp",EDGE,"E9.7.0"),sQuery(id+"F0.wireOp",EDGE,"E9.7.1"),sQuery(id+"F0.wireOp",EDGE,"E9.7.2"),sQuery(id+"F0.wireOp",EDGE,"E9.7.3"),sQuery(id+"F0.wireOp",EDGE,"E9.7.4"),sQuery(id+"F0.wireOp",EDGE,"E9.7.5"),sQuery(id+"F0.wireOp",EDGE,"E9.8.0"),sQuery(id+"F0.wireOp",EDGE,"E9.8.1"),sQuery(id+"F0.wireOp",EDGE,"E9.8.2"),sQuery(id+"F0.wireOp",EDGE,"E9.8.3"),sQuery(id+"F0.wireOp",EDGE,"E9.8.4"),sQuery(id+"F0.wireOp",EDGE,"E9.8.5"),sQuery(id+"F0.wireOp",EDGE,"E9.9.0"),sQuery(id+"F0.wireOp",EDGE,"E9.9.1"),sQuery(id+"F0.wireOp",EDGE,"E9.9.2"),sQuery(id+"F0.wireOp",EDGE,"E9.9.3"),sQuery(id+"F0.wireOp",EDGE,"E9.9.4"),sQuery(id+"F0.wireOp",EDGE,"E9.9.5"),sQuery(id+"F0.wireOp",EDGE,"E9.10.0"),sQuery(id+"F0.wireOp",EDGE,"E9.10.1"),sQuery(id+"F0.wireOp",EDGE,"E9.10.2"),sQuery(id+"F0.wireOp",EDGE,"E9.10.3"),sQuery(id+"F0.wireOp",EDGE,"E9.10.4"),sQuery(id+"F0.wireOp",EDGE,"E9.10.5"),sQuery(id+"F0.wireOp",EDGE,"E9.11.0"),sQuery(id+"F0.wireOp",EDGE,"E9.11.1"),sQuery(id+"F0.wireOp",EDGE,"E9.11.2"),sQuery(id+"F0.wireOp",EDGE,"E9.11.3"),sQuery(id+"F0.wireOp",EDGE,"E9.11.4"),sQuery(id+"F0.wireOp",EDGE,"E9.11.5"),sQuery(id+"F0.wireOp",EDGE,"E9.12.0"),sQuery(id+"F0.wireOp",EDGE,"E9.12.1"),sQuery(id+"F0.wireOp",EDGE,"E9.12.2"),sQuery(id+"F0.wireOp",EDGE,"E9.12.3"),sQuery(id+"F0.wireOp",EDGE,"E9.12.4"),sQuery(id+"F0.wireOp",EDGE,"E9.12.5"),sQuery(id+"F0.wireOp",EDGE,"E9.13.0"),sQuery(id+"F0.wireOp",EDGE,"E9.13.1"),sQuery(id+"F0.wireOp",EDGE,"E9.13.2"),sQuery(id+"F0.wireOp",EDGE,"E9.13.3"),sQuery(id+"F0.wireOp",EDGE,"E9.13.4"),sQuery(id+"F0.wireOp",EDGE,"E9.13.5"),sQuery(id+"F0.wireOp",EDGE,"E9.14.0"),sQuery(id+"F0.wireOp",EDGE,"E9.14.1"),sQuery(id+"F0.wireOp",EDGE,"E9.14.2"),sQuery(id+"F0.wireOp",EDGE,"E9.14.3"),sQuery(id+"F0.wireOp",EDGE,"E9.14.4"),sQuery(id+"F0.wireOp",EDGE,"E9.14.5"),sQuery(id+"F0.wireOp",EDGE,"E9.15.0"),sQuery(id+"F0.wireOp",EDGE,"E9.15.1"),sQuery(id+"F0.wireOp",EDGE,"E9.15.2"),sQuery(id+"F0.wireOp",EDGE,"E9.15.3"),sQuery(id+"F0.wireOp",EDGE,"E9.15.4"),sQuery(id+"F0.wireOp",EDGE,"E9.15.5"),sQuery(id+"F0.wireOp",EDGE,"E9.16.0"),sQuery(id+"F0.wireOp",EDGE,"E9.16.1"),sQuery(id+"F0.wireOp",EDGE,"E9.16.2"),sQuery(id+"F0.wireOp",EDGE,"E9.16.3"),sQuery(id+"F0.wireOp",EDGE,"E9.16.4"),sQuery(id+"F0.wireOp",EDGE,"E9.16.5"),sQuery(id+"F0.wireOp",EDGE,"E9.17.0"),sQuery(id+"F0.wireOp",EDGE,"E9.17.1"),sQuery(id+"F0.wireOp",EDGE,"E9.17.2"),sQuery(id+"F0.wireOp",EDGE,"E9.17.3"),sQuery(id+"F0.wireOp",EDGE,"E9.17.4"),sQuery(id+"F0.wireOp",EDGE,"E9.17.5"),sQuery(id+"F0.wireOp",EDGE,"E9.18.0"),sQuery(id+"F0.wireOp",EDGE,"E9.18.1"),sQuery(id+"F0.wireOp",EDGE,"E9.18.2"),sQuery(id+"F0.wireOp",EDGE,"E9.18.3"),sQuery(id+"F0.wireOp",EDGE,"E9.18.4"),sQuery(id+"F0.wireOp",EDGE,"E9.18.5"),sQuery(id+"F0.wireOp",EDGE,"E9.19.0"),sQuery(id+"F0.wireOp",EDGE,"E9.19.1"),sQuery(id+"F0.wireOp",EDGE,"E9.19.2"),sQuery(id+"F0.wireOp",EDGE,"E9.19.3"),sQuery(id+"F0.wireOp",EDGE,"E9.19.4"),sQuery(id+"F0.wireOp",EDGE,"E9.19.5"),sQuery(id+"F0.wireOp",EDGE,"E9.20.0"),sQuery(id+"F0.wireOp",EDGE,"E9.20.1"),sQuery(id+"F0.wireOp",EDGE,"E9.20.2"),sQuery(id+"F0.wireOp",EDGE,"E9.20.3"),sQuery(id+"F0.wireOp",EDGE,"E9.20.4"),sQuery(id+"F0.wireOp",EDGE,"E9.20.5"),sQuery(id+"F0.wireOp",EDGE,"E9.21.0"),sQuery(id+"F0.wireOp",EDGE,"E9.21.1"),sQuery(id+"F0.wireOp",EDGE,"E9.21.2"),sQuery(id+"F0.wireOp",EDGE,"E9.21.3"),sQuery(id+"F0.wireOp",EDGE,"E9.21.4"),sQuery(id+"F0.wireOp",EDGE,"E9.21.5"),sQuery(id+"F0.wireOp",EDGE,"E9.22.0"),sQuery(id+"F0.wireOp",EDGE,"E9.22.1"),sQuery(id+"F0.wireOp",EDGE,"E9.22.2"),sQuery(id+"F0.wireOp",EDGE,"E9.22.3"),sQuery(id+"F0.wireOp",EDGE,"E9.22.4"),sQuery(id+"F0.wireOp",EDGE,"E9.22.5"),sQuery(id+"F0.wireOp",EDGE,"E9.23.0"),sQuery(id+"F0.wireOp",EDGE,"E9.23.1"),sQuery(id+"F0.wireOp",EDGE,"E9.23.2"),sQuery(id+"F0.wireOp",EDGE,"E9.23.3"),sQuery(id+"F0.wireOp",EDGE,"E9.23.4"),sQuery(id+"F0.wireOp",EDGE,"E9.23.5"),sQuery(id+"F0.wireOp",EDGE,"E9.24.0"),sQuery(id+"F0.wireOp",EDGE,"E9.24.1"),sQuery(id+"F0.wireOp",EDGE,"E9.24.2"),sQuery(id+"F0.wireOp",EDGE,"E9.24.3"),sQuery(id+"F0.wireOp",EDGE,"E9.24.4"),sQuery(id+"F0.wireOp",EDGE,"E9.24.5"),sQuery(id+"F0.wireOp",EDGE,"E9.25.0"),sQuery(id+"F0.wireOp",EDGE,"E9.25.1"),sQuery(id+"F0.wireOp",EDGE,"E9.25.2"),sQuery(id+"F0.wireOp",EDGE,"E9.25.3"),sQuery(id+"F0.wireOp",EDGE,"E9.25.4"),sQuery(id+"F0.wireOp",EDGE,"E9.25.5"),sQuery(id+"F0.wireOp",EDGE,"E9.26.0"),sQuery(id+"F0.wireOp",EDGE,"E9.26.1"),sQuery(id+"F0.wireOp",EDGE,"E9.26.2"),sQuery(id+"F0.wireOp",EDGE,"E9.26.3"),sQuery(id+"F0.wireOp",EDGE,"E9.26.4"),sQuery(id+"F0.wireOp",EDGE,"E9.26.5"),sQuery(id+"F0.wireOp",EDGE,"E9.27.0"),sQuery(id+"F0.wireOp",EDGE,"E9.27.1"),sQuery(id+"F0.wireOp",EDGE,"E9.27.2"),sQuery(id+"F0.wireOp",EDGE,"E9.27.3"),sQuery(id+"F0.wireOp",EDGE,"E9.27.4"),sQuery(id+"F0.wireOp",EDGE,"E9.27.5"),sQuery(id+"F0.wireOp",EDGE,"E9.28.0"),sQuery(id+"F0.wireOp",EDGE,"E9.28.1"),sQuery(id+"F0.wireOp",EDGE,"E9.28.2"),sQuery(id+"F0.wireOp",EDGE,"E9.28.3"),sQuery(id+"F0.wireOp",EDGE,"E9.28.4"),sQuery(id+"F0.wireOp",EDGE,"E9.28.5"),sQuery(id+"F0.wireOp",EDGE,"E9.29.0"),sQuery(id+"F0.wireOp",EDGE,"E9.29.1"),sQuery(id+"F0.wireOp",EDGE,"E9.29.2"),sQuery(id+"F0.wireOp",EDGE,"E9.29.3"),sQuery(id+"F0.wireOp",EDGE,"E9.29.4"),sQuery(id+"F0.wireOp",EDGE,"E9.29.5"),sQuery(id+"F0.wireOp",EDGE,"E9.30.0"),sQuery(id+"F0.wireOp",EDGE,"E9.30.1"),sQuery(id+"F0.wireOp",EDGE,"E9.30.2"),sQuery(id+"F0.wireOp",EDGE,"E9.30.3"),sQuery(id+"F0.wireOp",EDGE,"E9.30.4"),sQuery(id+"F0.wireOp",EDGE,"E9.30.5"),sQuery(id+"F0.wireOp",EDGE,"E9.31.0"),sQuery(id+"F0.wireOp",EDGE,"E9.31.1"),sQuery(id+"F0.wireOp",EDGE,"E9.31.2"),sQuery(id+"F0.wireOp",EDGE,"E9.31.3"),sQuery(id+"F0.wireOp",EDGE,"E9.31.4"),sQuery(id+"F0.wireOp",EDGE,"E9.31.5"),sQuery(id+"F0.wireOp",EDGE,"E9.32.0"),sQuery(id+"F0.wireOp",EDGE,"E9.32.1"),sQuery(id+"F0.wireOp",EDGE,"E9.32.2"),sQuery(id+"F0.wireOp",EDGE,"E9.32.3"),sQuery(id+"F0.wireOp",EDGE,"E9.32.4"),sQuery(id+"F0.wireOp",EDGE,"E9.32.5"),sQuery(id+"F0.wireOp",EDGE,"E9.33.0"),sQuery(id+"F0.wireOp",EDGE,"E9.33.1"),sQuery(id+"F0.wireOp",EDGE,"E9.33.2"),sQuery(id+"F0.wireOp",EDGE,"E9.33.3"),sQuery(id+"F0.wireOp",EDGE,"E9.33.4"),sQuery(id+"F0.wireOp",EDGE,"E9.33.5"),sQuery(id+"F0.wireOp",EDGE,"E9.34.0"),sQuery(id+"F0.wireOp",EDGE,"E9.34.1"),sQuery(id+"F0.wireOp",EDGE,"E9.34.2"),sQuery(id+"F0.wireOp",EDGE,"E9.34.3"),sQuery(id+"F0.wireOp",EDGE,"E9.34.4"),sQuery(id+"F0.wireOp",EDGE,"E9.34.5"),sQuery(id+"F0.wireOp",EDGE,"E9.35.0"),sQuery(id+"F0.wireOp",EDGE,"E9.35.1"),sQuery(id+"F0.wireOp",EDGE,"E9.35.2"),sQuery(id+"F0.wireOp",EDGE,"E9.35.3"),sQuery(id+"F0.wireOp",EDGE,"E9.35.4"),sQuery(id+"F0.wireOp",EDGE,"E9.35.5"),sQuery(id+"F0.wireOp",EDGE,"E9.36.0"),sQuery(id+"F0.wireOp",EDGE,"E9.36.1"),sQuery(id+"F0.wireOp",EDGE,"E9.36.2"),sQuery(id+"F0.wireOp",EDGE,"E9.36.3"),sQuery(id+"F0.wireOp",EDGE,"E9.36.4"),sQuery(id+"F0.wireOp",EDGE,"E9.36.5"),sQuery(id+"F0.wireOp",EDGE,"E9.37.0"),sQuery(id+"F0.wireOp",EDGE,"E9.37.1"),sQuery(id+"F0.wireOp",EDGE,"E9.37.2"),sQuery(id+"F0.wireOp",EDGE,"E9.37.3"),sQuery(id+"F0.wireOp",EDGE,"E9.37.4"),sQuery(id+"F0.wireOp",EDGE,"E9.37.5"),sQuery(id+"F0.wireOp",EDGE,"E9.38.0"),sQuery(id+"F0.wireOp",EDGE,"E9.38.1"),sQuery(id+"F0.wireOp",EDGE,"E9.38.2"),sQuery(id+"F0.wireOp",EDGE,"E9.38.3"),sQuery(id+"F0.wireOp",EDGE,"E9.38.4"),sQuery(id+"F0.wireOp",EDGE,"E9.38.5"),sQuery(id+"F0.wireOp",EDGE,"E9.39.0"),sQuery(id+"F0.wireOp",EDGE,"E9.39.1"),sQuery(id+"F0.wireOp",EDGE,"E9.39.2"),sQuery(id+"F0.wireOp",EDGE,"E9.39.3"),sQuery(id+"F0.wireOp",EDGE,"E9.39.4"),sQuery(id+"F0.wireOp",EDGE,"E9.39.5"),sQuery(id+"F0.wireOp",EDGE,"E9.40.0"),sQuery(id+"F0.wireOp",EDGE,"E9.40.1"),sQuery(id+"F0.wireOp",EDGE,"E9.40.2"),sQuery(id+"F0.wireOp",EDGE,"E9.40.3"),sQuery(id+"F0.wireOp",EDGE,"E9.40.4"),sQuery(id+"F0.wireOp",EDGE,"E9.40.5"),sQuery(id+"F0.wireOp",EDGE,"E9.41.0"),sQuery(id+"F0.wireOp",EDGE,"E9.41.1"),sQuery(id+"F0.wireOp",EDGE,"E9.41.2"),sQuery(id+"F0.wireOp",EDGE,"E9.41.3"),sQuery(id+"F0.wireOp",EDGE,"E9.41.4"),sQuery(id+"F0.wireOp",EDGE,"E9.41.5"),sQuery(id+"F0.wireOp",EDGE,"E9.42.0"),sQuery(id+"F0.wireOp",EDGE,"E9.42.1"),sQuery(id+"F0.wireOp",EDGE,"E9.42.2"),sQuery(id+"F0.wireOp",EDGE,"E9.42.3"),sQuery(id+"F0.wireOp",EDGE,"E9.42.4"),sQuery(id+"F0.wireOp",EDGE,"E9.42.5"),sQuery(id+"F0.wireOp",EDGE,"E9.43.0"),sQuery(id+"F0.wireOp",EDGE,"E9.43.1"),sQuery(id+"F0.wireOp",EDGE,"E9.43.2"),sQuery(id+"F0.wireOp",EDGE,"E9.43.3"),sQuery(id+"F0.wireOp",EDGE,"E9.43.4"),sQuery(id+"F0.wireOp",EDGE,"E9.43.5"),sQuery(id+"F0.wireOp",EDGE,"E9.44.0"),sQuery(id+"F0.wireOp",EDGE,"E9.44.1"),sQuery(id+"F0.wireOp",EDGE,"E9.44.2"),sQuery(id+"F0.wireOp",EDGE,"E9.44.3"),sQuery(id+"F0.wireOp",EDGE,"E9.44.4"),sQuery(id+"F0.wireOp",EDGE,"E9.44.5"),sQuery(id+"F0.wireOp",EDGE,"E9.45.0"),sQuery(id+"F0.wireOp",EDGE,"E9.45.1"),sQuery(id+"F0.wireOp",EDGE,"E9.45.2"),sQuery(id+"F0.wireOp",EDGE,"E9.45.3"),sQuery(id+"F0.wireOp",EDGE,"E9.45.4"),sQuery(id+"F0.wireOp",EDGE,"E9.45.5"),sQuery(id+"F0.wireOp",EDGE,"E9.46.0"),sQuery(id+"F0.wireOp",EDGE,"E9.46.1"),sQuery(id+"F0.wireOp",EDGE,"E9.46.2"),sQuery(id+"F0.wireOp",EDGE,"E9.46.3"),sQuery(id+"F0.wireOp",EDGE,"E9.46.4"),sQuery(id+"F0.wireOp",EDGE,"E9.46.5"),sQuery(id+"F0.wireOp",EDGE,"E9.47.0"),sQuery(id+"F0.wireOp",EDGE,"E9.47.1"),sQuery(id+"F0.wireOp",EDGE,"E9.47.2"),sQuery(id+"F0.wireOp",EDGE,"E9.47.3"),sQuery(id+"F0.wireOp",EDGE,"E9.47.4"),sQuery(id+"F0.wireOp",EDGE,"E9.47.5"),sQuery(id+"F0.wireOp",EDGE,"E10.trimOffspring"),sQuery(id+"F0.wireOp",EDGE,"E11.trimOffspring"),sQuery(id+"F0.wireOp",EDGE,"E12.trimOffspring"),sQuery(id+"F0.wireOp",EDGE,"E13.trimOffspring"),sQuery(id+"F0.wireOp",EDGE,"E14.trimOffspring"),sQuery(id+"F0.wireOp",EDGE,"E15.trimOffspring"),sQuery(id+"F0.wireOp",EDGE,"E16.trimOffspring"),sQuery(id+"F0.wireOp",EDGE,"E17.trimOffspring"),sQuery(id+"F0.wireOp",EDGE,"E18.trimOffspring"),sQuery(id+"F0.wireOp",EDGE,"E19.trimOffspring"),sQuery(id+"F0.wireOp",EDGE,"E20.trimOffspring"),sQuery(id+"F0.wireOp",EDGE,"E21.trimOffspring"),sQuery(id+"F0.wireOp",EDGE,"E22.trimOffspring"),sQuery(id+"F0.wireOp",EDGE,"E23.trimOffspring"),sQuery(id+"F0.wireOp",EDGE,"E24.trimOffspring"),sQuery(id+"F0.wireOp",EDGE,"E25.trimOffspring"),sQuery(id+"F0.wireOp",EDGE,"E26.trimOffspring"),sQuery(id+"F0.wireOp",EDGE,"E27.trimOffspring"),sQuery(id+"F0.wireOp",EDGE,"E28.trimOffspring"),sQuery(id+"F0.wireOp",EDGE,"E29.trimOffspring"),sQuery(id+"F0.wireOp",EDGE,"E30.trimOffspring"),sQuery(id+"F0.wireOp",EDGE,"E31.trimOffspring"),sQuery(id+"F0.wireOp",EDGE,"E32.trimOffspring"),sQuery(id+"F0.wireOp",EDGE,"E33.trimOffspring"),sQuery(id+"F0.wireOp",EDGE,"E34.trimOffspring"),sQuery(id+"F0.wireOp",EDGE,"E35.trimOffspring"),sQuery(id+"F0.wireOp",EDGE,"E36.trimOffspring"),sQuery(id+"F0.wireOp",EDGE,"E37.trimOffspring"),sQuery(id+"F0.wireOp",EDGE,"E38.trimOffspring"),sQuery(id+"F0.wireOp",EDGE,"E39.trimOffspring"),sQuery(id+"F0.wireOp",EDGE,"E40.trimOffspring"),sQuery(id+"F0.wireOp",EDGE,"E41.trimOffspring"),sQuery(id+"F0.wireOp",EDGE,"E42.trimOffspring"),sQuery(id+"F0.wireOp",EDGE,"E43.trimOffspring"),sQuery(id+"F0.wireOp",EDGE,"E44.trimOffspring"),sQuery(id+"F0.wireOp",EDGE,"E45.trimOffspring"),sQuery(id+"F0.wireOp",EDGE,"E46.trimOffspring"),sQuery(id+"F0.wireOp",EDGE,"E47.trimOffspring"),sQuery(id+"F0.wireOp",EDGE,"E48.trimOffspring"),sQuery(id+"F0.wireOp",EDGE,"E49.trimOffspring"),sQuery(id+"F0.wireOp",EDGE,"E50.trimOffspring"),sQuery(id+"F0.wireOp",EDGE,"E51.trimOffspring"),sQuery(id+"F0.wireOp",EDGE,"E52.trimOffspring"),sQuery(id+"F0.wireOp",EDGE,"E53.trimOffspring"),sQuery(id+"F0.wireOp",EDGE,"E54.trimOffspring"),sQuery(id+"F0.wireOp",EDGE,"E55.trimOffspring")])],"isStart":true});
            var sketch = newSketch(context, id + "F4", { "sketchPlane" : qUnion([Q0])});
            skCircle(sketch, "E57", {"center": v(0, 0) * mm, "radius": 15.5 * mm});
            skSolve(sketch);
        }
        {
            var Q0;
            Q0=makeQuery(id+"F4.imprint","IMPRINT",FACE,{"disambiguationData":[TD([[makeQuery(id+"F4.imprint","IMPRINT",EDGE,{"derivedFrom":makeQuery(id+"F1.opExtrude","CAP_EDGE",EDGE,{"disambiguationData":[OSD([sQuery(id+"F0.wireOp",EDGE,"E0")])],"isStart":true})}),-1.0]])]});
            var Q1;
            Q1=makeQuery(id+"F4.imprint","IMPRINT",FACE,{"disambiguationData":[TD([[makeQuery(id+"F4.imprint","IMPRINT",EDGE,{"derivedFrom":sQuery(id+"F4.wireOp",EDGE,"E57")}),1.0]])]});
            extrude(context, id + "F5", {"entities" : qUnion([Q0, Q1]), "operationType" : NewBodyOperationType.ADD, "depth" : .5 * mm, "offsetDistance" : 25 * mm});
        }
        {
            var Q0;
            Q0=makeQuery(id+"F3.opExtrude","CAP_FACE",FACE,{"disambiguationData":[OSD([sQuery(id+"F2.wireOp",EDGE,"E56")])],"isStart":false});
            var sketch = newSketch(context, id + "F6", { "sketchPlane" : qUnion([Q0])});
            skCircle(sketch, "E58", {"center": v(0, 0) * mm, "radius": 3.98 * mm});
            skCircle(sketch, "E59", {"center": v(0, 0) * mm, "radius": 3.18 * mm});
            skSolve(sketch);
        }
        {
            var Q0;
            Q0=makeQuery(id+"F6.imprint","IMPRINT",FACE,{"disambiguationData":[TD([[makeQuery(id+"F6.imprint","IMPRINT",EDGE,{"derivedFrom":sQuery(id+"F6.wireOp",EDGE,"E58")}),1.0]])]});
            extrude(context, id + "F7", {"entities" : qUnion([Q0]), "operationType" : NewBodyOperationType.ADD, "depth" : 40 * mm, "offsetDistance" : 25 * mm});
        }
        {
            var Q0;
            Q0=qCreatedBy(makeId("Right.planeOp"),FACE);
            var sketch = newSketch(context, id + "F8", { "sketchPlane" : qUnion([Q0])});
            skLineSegment(sketch, "E60", {"start": v(3.98, 47) * mm, "end": v(3.98, 7) * mm});
            skLineSegment(sketch, "E61.bottom", {"start": v(3.98, 32.75) * mm, "end": v(1.47, 32.75) * mm});
            skLineSegment(sketch, "E61.top", {"start": v(3.98, 26.25) * mm, "end": v(1.47, 26.25) * mm});
            skLineSegment(sketch, "E61.left", {"start": v(3.98, 32.75) * mm, "end": v(3.98, 26.25) * mm});
            skLineSegment(sketch, "E61.right", {"start": v(1.48, 32.75) * mm, "end": v(1.48, 26.25) * mm});
            skSolve(sketch);
        }
        {
            var Q0;
            {var subQ2=sQuery(id+"F8.wireOp",EDGE,"E61.bottom");Q0=makeQuery(id+"F8.imprint","IMPRINT",FACE,{"disambiguationData":[TD([[makeQuery(id+"F8.imprint","IMPRINT",EDGE,{"derivedFrom":subQ2}),1.0]])]});}
            extrude(context, id + "F9", {"entities" : qUnion([Q0]), "operationType" : NewBodyOperationType.REMOVE, "endBound" : BoundingType.THROUGH_ALL, "oppositeDirection" : true, "depth" : 25 * mm, "offsetDistance" : 25 * mm, "hasSecondDirection" : true, "secondDirectionOppositeDirection" : false, "secondDirectionDepth" : 25 * mm});
        }
    });
